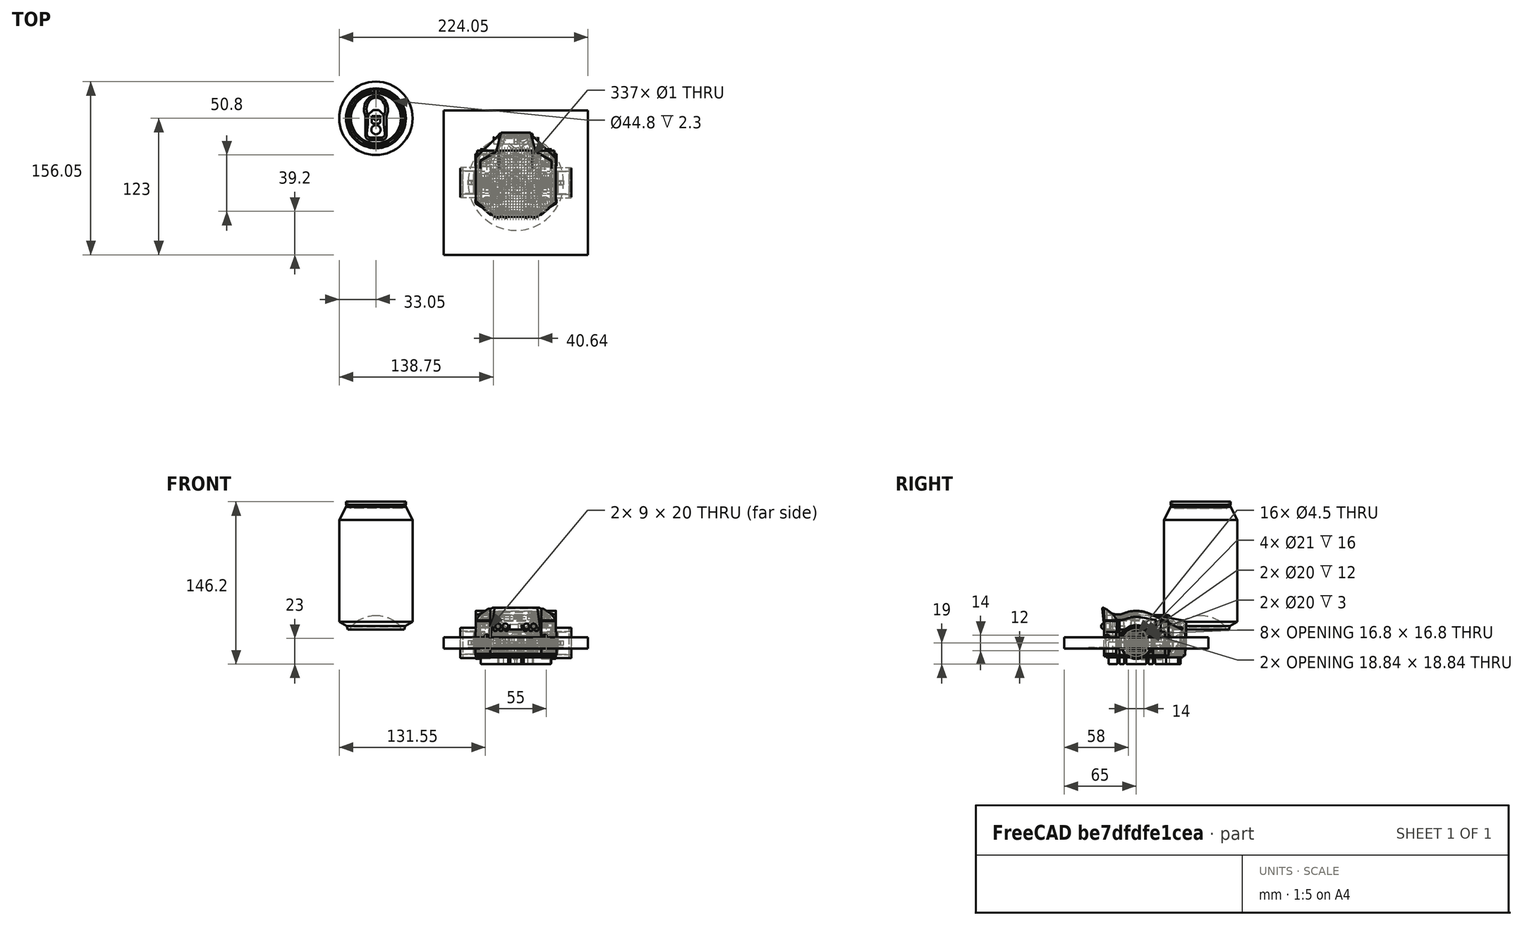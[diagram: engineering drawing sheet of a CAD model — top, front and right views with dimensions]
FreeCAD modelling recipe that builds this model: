
FCSTD DOCUMENT  (FreeCAD 0.16R)
Label: rat
License: All rights reserved
LicenseURL: http://en.wikipedia.org/wiki/All_rights_reserved
objects: Part::Cylinder×68, Part::MultiFuse×43, Part::Feature×36, Part::Cut×36, Sketcher::SketchObject×36, PartDesign::Pad×34, Part::FeaturePython×31, Part::Box×18, Part::Fillet×15, Part::Mirroring×12, Part::Chamfer×7, Part::MultiCommon×4, Image::ImagePlane×3, App::DocumentObjectGroup×3, Part::Sphere×1, Part::Compound×1
note: 376 computed .brp shape members not serialized (recipe doc carries the construction recipe); baked Part::Feature solids carry a one-line shape summary decoded from their .brp

FEATURE [Part::Feature] Part__Feature  label="Pololu - 1_250 Micro gear motor"
  shape: bbox 12 x 10 x 1 mm, 20 faces (baked)
FEATURE [Part::Feature] Part__Feature001  label="Pololu - 1_250 Micro gear motor001"
  shape: bbox 1 x 1 x 8 mm, 7 faces (baked)
FEATURE [Part::Feature] Part__Feature002  label="Pololu - 1_250 Micro gear motor002"
  shape: bbox 1 x 1 x 8 mm, 7 faces (baked)
FEATURE [Part::Feature] Part__Feature003  label="Pololu - 1_250 Micro gear motor003"
  shape: bbox 2 x 2 x 3 mm, 6 faces (baked)
FEATURE [Part::Feature] Part__Feature004  label="Pololu - 1_250 Micro gear motor004"
  shape: bbox 3 x 3 x 2 mm, 6 faces (baked)
FEATURE [Part::Feature] Part__Feature005  label="Pololu - 1_250 Micro gear motor005"
  shape: bbox 3 x 3 x 2 mm, 6 faces (baked)
FEATURE [Part::Feature] Part__Feature006  label="Pololu - 1_250 Micro gear motor006"
  shape: bbox 3 x 3 x 4 mm, 6 faces (baked)
FEATURE [Part::Feature] Part__Feature007  label="Pololu - 1_250 Micro gear motor007"
  shape: bbox 3 x 3 x 4 mm, 6 faces (baked)
FEATURE [Part::Feature] Part__Feature008  label="Pololu - 1_250 Micro gear motor008"
  shape: bbox 2 x 2 x 1.5 mm, 6 faces (baked)
FEATURE [Part::Feature] Part__Feature009  label="Pololu - 1_250 Micro gear motor009"
  shape: bbox 5.5 x 5.5 x 0.75 mm, 6 faces (baked)
FEATURE [Part::Feature] Part__Feature010  label="Pololu - 1_250 Micro gear motor010"
  shape: bbox 12 x 10 x 1 mm, 22 faces (baked)
FEATURE [Part::Feature] Part__Feature011  label="Pololu - 1_250 Micro gear motor011"
  shape: bbox 5.5 x 5.5 x 1 mm, 6 faces (baked)
FEATURE [Part::Feature] Part__Feature012  label="Pololu - 1_250 Micro gear motor012"
  shape: bbox 5.5 x 5.5 x 0.75 mm, 6 faces (baked)
FEATURE [Part::Feature] Part__Feature013  label="Pololu - 1_250 Micro gear motor013"
  shape: bbox 2 x 2 x 1.15 mm, 6 faces (baked)
FEATURE [Part::Feature] Part__Feature014  label="Pololu - 1_250 Micro gear motor014"
  shape: bbox 5.5 x 5.5 x 1 mm, 6 faces (baked)
FEATURE [Part::Feature] Part__Feature015  label="Pololu - 1_250 Micro gear motor015"
  shape: bbox 2 x 2 x 1.3 mm, 6 faces (baked)
FEATURE [Part::Feature] Part__Feature016  label="Pololu - 1_250 Micro gear motor016"
  shape: bbox 2.94 x 2.94 x 18.27 mm, 12 faces (baked)
FEATURE [Part::Feature] Part__Feature017  label="Pololu - 1_250 Micro gear motor017"
  shape: bbox 12 x 10 x 1.6 mm, 37 faces (baked)
FEATURE [Part::Feature] Part__Feature018  label="Pololu - 1_250 Micro gear motor018"
  shape: bbox 12 x 10 x 14 mm, 11 faces (baked)
FEATURE [Part::Feature] Part__Feature019  label="Pololu - 1_250 Micro gear motor019"
  shape: bbox 12 x 10 x 2.5 mm, 14 faces (baked)
FEATURE [Part::Feature] Part__Feature020  label="Pololu - 1_250 Micro gear motor020"
  shape: bbox 0.3 x 1.5 x 2 mm, 8 faces (baked)
FEATURE [Part::Feature] Part__Feature021  label="Pololu - 1_250 Micro gear motor021"
  shape: bbox 0.3 x 1.5 x 2 mm, 8 faces (baked)
FEATURE [Part::Feature] Part__Feature022  label="Pololu - 1_250 Micro gear motor022"
  shape: bbox 2.65 x 2.65 x 8.95 mm, 21 faces (baked)
FEATURE [Part::Feature] Part__Feature023  label="Pololu - 1_250 Micro gear motor023"
  shape: bbox 2.65 x 2.65 x 8.95 mm, 21 faces (baked)
FEATURE [Part::MultiFuse] Fusion  label="motor-src"
  Shapes = -> [Part__Feature,Part__Feature001,Part__Feature002,Part__Feature003,Part__Feature004,Part__Feature005,Part__Feature006,Part__Feature007,Part__Feature008,Part__Feature009,Part__Feature010,Part__Feature011,Part__Feature012,Part__Feature013,Part__Feature014,Part__Feature015,Part__Feature016,Part__Feature017,Part__Feature018,Part__Feature019,Part__Feature020,Part__Feature021,Part__Feature022,+1 more]
FEATURE [Part::FeaturePython] Clone  label="left-motor"  # Draft clone (typed FeaturePython)
  Objects = -> [Fusion]
  Placement = pos=(-14.5,0,5) rot=(0,-1,0;1.5708rad)
  Scale = (1,1,1)
FEATURE [Part::FeaturePython] Clone001  label="right-motor"  # Draft clone (typed FeaturePython)
  Objects = -> [Fusion]
  Placement = pos=(14.5,0,5) rot=(0,1,0;1.5708rad)
  Scale = (1,1,1)
FEATURE [Part::Cylinder] Cylinder
  Angle = 360
  Height = 16
  Radius = 13.75
FEATURE [Part::Cylinder] Cylinder001
  Angle = 360
  Height = 20
  Placement = pos=(0,0,-1) rot=(0,0,1;0rad)
  Radius = 10.5
FEATURE [Part::Cut] Cut
  Base = -> Cylinder
  Tool = -> Cylinder001
FEATURE [Part::Fillet] Fillet  label="tire-src"
  Base = -> Cut
  Edges = 2 edges r=1: [Edge1,Edge3]
FEATURE [Part::Cylinder] Cylinder002
  Angle = 360
  Height = 16
  Radius = 10.5
FEATURE [Part::Cylinder] Cylinder003
  Angle = 360
  Height = 16
  Placement = pos=(0,0,4) rot=(0,0,1;0rad)
  Radius = 9.8
FEATURE [Part::Cut] Cut001
  Base = -> Cylinder002
  Tool = -> Cylinder003
FEATURE [Part::FeaturePython] Clone002  label="Clone of tire-src"  # Draft clone (typed FeaturePython)
  Objects = -> [Fillet]
  Placement = pos=(-32,0,5) rot=(0,-1,0;1.5708rad)
  Scale = (1,1,1)
FEATURE [Part::FeaturePython] Clone004  label="Clone of tire-src001"  # Draft clone (typed FeaturePython)
  Objects = -> [Fillet]
  Placement = pos=(32,0,5) rot=(0,1,0;1.5708rad)
  Scale = (1,1,1)
FEATURE [Part::Box] Box  label="Cube"
  Height = 10
  Length = 130
  Placement = pos=(-65,-65,0) rot=(0,0,1;0rad)
  Width = 130
FEATURE [Part::Cylinder] Cylinder004
  Angle = 360
  Height = 1
  Radius = 43
FEATURE [Part::Feature] Part__Feature024  label="felga_solarbotics"
  shape: bbox 20.38 x 20.38 x 13.12 mm, 25 faces (baked)
FEATURE [Part::Feature] Part__Feature025  label="opona solarbotics"
  shape: bbox 28.6 x 28.6 x 12.96 mm, 18 faces (baked)
FEATURE [Part::FeaturePython] Clone006  label="left_wheel"  # Draft clone (typed FeaturePython)
  Objects = -> [Part__Feature024]
  Placement = pos=(-36,0,5) rot=(0,1,0;1.5708rad)
  Scale = (1,1,1)
FEATURE [Part::FeaturePython] Clone007  label="left_tire"  # Draft clone (typed FeaturePython)
  Objects = -> [Part__Feature025]
  Placement = pos=(-36,0,5) rot=(0,1,0;1.5708rad)
  Scale = (1,1,1)
FEATURE [Part::FeaturePython] Clone008  label="right_wheel"  # Draft clone (typed FeaturePython)
  Objects = -> [Part__Feature024]
  Placement = pos=(36,0,5) rot=(0,-1,0;1.5708rad)
  Scale = (1,1,1)
FEATURE [Part::FeaturePython] Clone009  label="right_tire"  # Draft clone (typed FeaturePython)
  Objects = -> [Part__Feature025]
  Placement = pos=(36,0,5) rot=(0,-1,0;1.5708rad)
  Scale = (1,1,1)
FEATURE [Part::Box] Box001  label="Cubo"
  Height = 17
  Length = 44
  Width = 12
FEATURE [Part::Box] Box002  label="Cube001"
  Height = 9
  Length = 22
  Placement = pos=(-11,-27.5,16) rot=(0,0,1;0rad)
  Width = 52
FEATURE [Sketcher::SketchObject] Sketch
  Placement = pos=(0,0,-6) rot=(0,0,1;0rad)
  sketch-geometry (23):
    g0: LineSegment StartX=-36.5 StartY=15 StartZ=0 EndX=-23 EndY=15 EndZ=0
    g1: LineSegment StartX=-23 StartY=15 StartZ=0 EndX=-23 EndY=-15 EndZ=0
    g2: LineSegment StartX=-23 StartY=-15 StartZ=0 EndX=-36.5 EndY=-15 EndZ=0
    g3: LineSegment StartX=36.5 StartY=-15 StartZ=0 EndX=23 EndY=-15 EndZ=0
    g4: LineSegment StartX=23 StartY=-15 StartZ=0 EndX=23 EndY=15 EndZ=0
    g5: LineSegment StartX=23 StartY=15 StartZ=0 EndX=36.5 EndY=15 EndZ=0
    g6: LineSegment [constr] StartX=-23 StartY=15 StartZ=0 EndX=23 EndY=15 EndZ=0
    g7: LineSegment [constr] StartX=-23 StartY=-15 StartZ=0 EndX=23 EndY=-15 EndZ=0
    g8: LineSegment StartX=-36.5 StartY=25.9507 StartZ=0 EndX=-24.3352 EndY=25.9507 EndZ=0
    g9: LineSegment StartX=-24.3352 StartY=25.9507 StartZ=0 EndX=-15 EndY=31.9395 EndZ=0
    g10: LineSegment StartX=15 StartY=31.9395 StartZ=0 EndX=24.3352 EndY=25.9507 EndZ=0
    g11: LineSegment StartX=24.3352 StartY=25.9507 StartZ=0 EndX=36.5 EndY=25.9507 EndZ=0
    g12: LineSegment [constr] StartX=-24.3352 StartY=25.9507 StartZ=0 EndX=24.3352 EndY=25.9507 EndZ=0
    g13: LineSegment StartX=-36.5 StartY=15 StartZ=0 EndX=-36.5 EndY=25.9507 EndZ=0
    g14: LineSegment StartX=-36.5 StartY=-15 StartZ=0 EndX=-36.5 EndY=-18.3134 EndZ=0
    g15: LineSegment StartX=36.5 StartY=25.9507 StartZ=0 EndX=36.5 EndY=15 EndZ=0
    g16: LineSegment StartX=-36.5 StartY=-18.3134 StartZ=0 EndX=-23 EndY=-26.9899 EndZ=0
    g17: LineSegment StartX=-23 StartY=-26.9899 StartZ=0 EndX=23 EndY=-26.9899 EndZ=0
    g18: LineSegment StartX=23 StartY=-26.9899 StartZ=0 EndX=36.5 EndY=-18.3134 EndZ=0
    g19: LineSegment StartX=36.5 StartY=-18.3134 StartZ=0 EndX=36.5 EndY=-15 EndZ=0
    g20: LineSegment StartX=-15 StartY=31.9395 StartZ=0 EndX=-15 EndY=44 EndZ=0
    g21: LineSegment StartX=-15 StartY=44 StartZ=0 EndX=15 EndY=44 EndZ=0
    g22: LineSegment StartX=15 StartY=44 StartZ=0 EndX=15 EndY=31.9395 EndZ=0
  constraints (61):
    c: Horizontal(g0)
    c: Coincident(g0,g1)
    c: Vertical(g1)
    c: Coincident(g1,g2)
    c: Horizontal(g2)
    c: Horizontal(g3)
    c: Coincident(g3,g4)
    c: Vertical(g4)
    c: Coincident(g4,g5)
    c: Horizontal(g5)
    c: Coincident(g6,g0)
    c: Coincident(g6,g4)
    c: Coincident(g7,g1)
    c: Horizontal(g7)
    c: Coincident(g7,g3)
    c: Equal(g1,g4)
    c: Distance(g4) = 30
    c: Symmetric(g4,g3,g-1)
    c: Distance(g0,g4) = 46
    c: Equal(g0,g5)
    c: Distance(g0) = 13.5
    c: Symmetric(g4,g0,g-2)
    c: Coincident(g8,g9)
    c: Coincident(g10,g11)
    c: Horizontal(g11)
    c: Horizontal(g8)
    c: Equal(g8,g11)
    c: Coincident(g12,g8)
    c: Coincident(g12,g10)
    c: Horizontal(g12)
    c: Symmetric(g8,g10,g-2)
    c: Symmetric(g9,g10,g-2)
    c: Equal(g3,g2)
    c: Equal(g2,g0)
    c: Coincident(g13,g0)
    c: Vertical(g13)
    c: Coincident(g2,g14)
    c: Vertical(g14)
    c: Coincident(g15,g5)
    c: Vertical(g15)
    c: Coincident(g11,g15)
    c: Coincident(g8,g13)
    c: Coincident(g14,g16)
    c: Coincident(g16,g17)
    c: Horizontal(g17)
    c: Coincident(g17,g18)
    c: Coincident(g18,g19)
    c: Vertical(g19)
    c: Coincident(g19,g3)
    c: Equal(g16,g18)
    c: Equal(g14,g19)
    c: Distance(g17) = 46
    c: Coincident(g9,g20)
    c: Vertical(g20)
    c: Coincident(g20,g21)
    c: Horizontal(g21)
    c: Coincident(g21,g22)
    c: Coincident(g22,g10)
    c: Vertical(g22)
    c: Distance(g21) = 30
    c: DistanceY(g-1,g20) = 44
FEATURE [PartDesign::Pad] Pad001
  Length = 21
  Length2 = 100
  Placement = pos=(0,0,-6) rot=(0,0,1;0rad)
  Sketch = -> Sketch
  Type = 0
FEATURE [Part::Cylinder] Cylinder005
  Angle = 360
  Height = 40
  Placement = pos=(-20,38,0) rot=(0,1,0;1.5708rad)
  Radius = 3
FEATURE [Part::Cylinder] Cylinder006
  Angle = 360
  Height = 40
  Placement = pos=(-20,38,9) rot=(0,1,0;1.5708rad)
  Radius = 3
FEATURE [Part::Cylinder] Cylinder007
  Angle = 360
  Height = 30
  Placement = pos=(-30,0,9) rot=(-1,0,0;1.5708rad)
  Radius = 3
FEATURE [Part::Cylinder] Cylinder008
  Angle = 360
  Height = 30
  Placement = pos=(-30,0,0) rot=(-1,0,0;1.5708rad)
  Radius = 3
FEATURE [Part::Cylinder] Cylinder009
  Angle = 360
  Height = 30
  Placement = pos=(30,0,9) rot=(-1,0,0;1.5708rad)
  Radius = 3
FEATURE [Part::Cylinder] Cylinder010
  Angle = 360
  Height = 30
  Placement = pos=(30,0,0) rot=(-1,0,0;1.5708rad)
  Radius = 3
FEATURE [Part::Cylinder] Cylinder011
  Angle = 360
  Height = 35
  Placement = pos=(7,16,9) rot=(-0.357407,0.862856,0.357407;1.71777rad)
  Radius = 3
FEATURE [Part::Cylinder] Cylinder012
  Angle = 360
  Height = 35
  Placement = pos=(7,16,0) rot=(-0.357407,0.862856,0.357407;1.71777rad)
  Radius = 3
FEATURE [Part::Cylinder] Cylinder013
  Angle = 360
  Height = 35
  Placement = pos=(-7,16,9) rot=(0.678599,-0.281084,-0.678598;3.68963rad)
  Radius = 3
FEATURE [Part::Cylinder] Cylinder014
  Angle = 360
  Height = 35
  Placement = pos=(-7,16,0) rot=(-0.678598,0.281085,0.678598;2.59356rad)
  Radius = 3
FEATURE [Part::MultiFuse] Fusion001
  Shapes = -> [Cylinder009,Cylinder013,Cylinder010,Cylinder012,Cylinder006,Cylinder008,Cylinder011,Cylinder005,Cylinder014,Cylinder007]
FEATURE [Part::Cut] Cut003
  Base = -> Pad001
  Tool = -> Fusion001
FEATURE [Part::Cylinder] Cylinder015  label="Cilindro"
  Angle = 360
  Height = 6.2
  Radius = 2.5
FEATURE [Part::Sphere] Sphere  label="Esféra"
  Angle1 = -90
  Angle2 = 90
  Angle3 = 180
  Placement = pos=(0,0,6.2) rot=(1,0,0;1.5708rad)
  Radius = 2.5
FEATURE [Part::Cylinder] Cylinder016  label="Cilindro001"
  Angle = 360
  Height = 1
  Radius = 2.9
FEATURE [Part::MultiFuse] Fusion002  label="Funda"
  Shapes = -> [Cylinder015,Cylinder016,Sphere]
FEATURE [Sketcher::SketchObject] Sketch002
  Placement = pos=(0,0,0) rot=(1,0,0;1.5708rad)
  sketch-geometry (9):
    g0: LineSegment StartX=-2.06901 StartY=-1.50757 StartZ=0 EndX=-2.06901 EndY=2.25482 EndZ=0
    g1: LineSegment StartX=-2.06901 StartY=2.25482 StartZ=0 EndX=-1.71216 EndY=2.25482 EndZ=0
    g2: LineSegment StartX=-1.71216 StartY=2.25482 StartZ=0 EndX=-1.71216 EndY=3.41819 EndZ=0
    g3: LineSegment StartX=-1.71216 StartY=3.41819 StartZ=0 EndX=1.35716 EndY=3.41819 EndZ=0
    g4: LineSegment StartX=1.35716 StartY=3.41819 StartZ=0 EndX=1.35716 EndY=3.07166 EndZ=0
    g5: LineSegment StartX=1.35716 StartY=3.07166 StartZ=0 EndX=-0.05374 EndY=1.66076 EndZ=0
    g6: LineSegment StartX=-0.05374 StartY=1.66076 StartZ=0 EndX=-1.56901 EndY=1.66076 EndZ=0
    g7: LineSegment StartX=-1.56901 StartY=1.66076 StartZ=0 EndX=-1.56901 EndY=-1.5 EndZ=0
    g8: LineSegment StartX=-1.56901 StartY=-1.5 StartZ=0 EndX=-2.06901 EndY=-1.50757 EndZ=0
  constraints (18):
    c: Vertical(g0)
    c: Coincident(g0,g1)
    c: Horizontal(g1)
    c: Coincident(g1,g2)
    c: Vertical(g2)
    c: Coincident(g2,g3)
    c: Horizontal(g3)
    c: Coincident(g3,g4)
    c: Vertical(g4)
    c: Coincident(g4,g5)
    c: Coincident(g5,g6)
    c: Horizontal(g6)
    c: Coincident(g6,g7)
    c: Vertical(g7)
    c: Coincident(g7,g8)
    c: Coincident(g8,g0)
    c: DistanceY(g-1,g7) = -1.5
    c: DistanceX(g0,g7) = 0.5
FEATURE [PartDesign::Pad] Pad002  label="Catodo"
  Length = 0.3
  Length2 = 100
  Placement = pos=(0,0,0) rot=(1,0,0;1.5708rad)
  Sketch = -> Sketch002
  Type = 0
FEATURE [Sketcher::SketchObject] Sketch003
  Placement = pos=(0,0,0) rot=(1,0,0;1.5708rad)
  sketch-geometry (7):
    g0: LineSegment StartX=2.0234 StartY=-1.57582 StartZ=0 EndX=2.0234 EndY=3.38927 EndZ=0
    g1: LineSegment StartX=2.0234 StartY=3.38927 StartZ=0 EndX=1.5234 EndY=3.36901 EndZ=0
    g2: LineSegment StartX=1.5234 StartY=3.36901 StartZ=0 EndX=1.5234 EndY=3.02449 EndZ=0
    g3: LineSegment StartX=1.5234 StartY=3.02449 StartZ=0 EndX=0.294592 EndY=1.68695 EndZ=0
    g4: LineSegment StartX=0.294592 StartY=1.68695 StartZ=0 EndX=1.51053 EndY=1.68695 EndZ=0
    g5: LineSegment StartX=1.51053 StartY=1.68695 StartZ=0 EndX=1.51053 EndY=-1.57582 EndZ=0
    g6: LineSegment StartX=1.51053 StartY=-1.57582 StartZ=0 EndX=2.0234 EndY=-1.57582 EndZ=0
  constraints (13):
    c: Vertical(g0)
    c: Coincident(g1,g0)
    c: DistanceX(g1,g0) = 0.5
    c: Coincident(g1,g2)
    c: Vertical(g2)
    c: Coincident(g2,g3)
    c: Coincident(g3,g4)
    c: Horizontal(g4)
    c: Coincident(g4,g5)
    c: Vertical(g5)
    c: Coincident(g5,g6)
    c: Coincident(g6,g0)
    c: Horizontal(g6)
FEATURE [PartDesign::Pad] Pad003  label="Anodo"
  Length = 0.3
  Length2 = 100
  Placement = pos=(0,0,0) rot=(1,0,0;1.5708rad)
  Sketch = -> Sketch003
  Type = 0
FEATURE [Part::MultiFuse] Fusion003  label="led-src"
  Shapes = -> [Fusion002,Pad003,Pad002]
FEATURE [Part::Box] Box003  label="Cube002"
  Height = 16
  Length = 30
  Placement = pos=(-15,-27,14) rot=(0,0,1;0rad)
  Width = 71
FEATURE [Part::Chamfer] Chamfer
  Base = -> Box003
  Edges = 1 edges r=15: [Edge12]
FEATURE [Part::MultiFuse] Fusion004
  Shapes = -> [Chamfer,Cut003]
FEATURE [Part::FeaturePython] Clone019  label="clone-lid"  # WARN: FeaturePython — macro-defined, semantics opaque (R4)
  Placement = pos=(0,0,110.4) rot=(0,0,1;3.14159rad)
  Scale = (1,1,1)
FEATURE [Part::FeaturePython] Clone020  label="clone-can"  # WARN: FeaturePython — macro-defined, semantics opaque (R4)
  Placement = pos=(0,0,0) rot=(1,0,0;1.5708rad)
  Scale = (1,1,1)
FEATURE [Sketcher::SketchObject] Sketch006
  Placement = pos=(36,0,1) rot=(0.57735,0.57735,0.57735;2.0944rad)
  sketch-geometry (9):
    g0: LineSegment StartX=-29 StartY=36 StartZ=0 EndX=-29 EndY=-8 EndZ=0
    g1: LineSegment StartX=-29 StartY=-8 StartZ=0 EndX=43 EndY=-8 EndZ=0
    g2: LineSegment StartX=43 StartY=-8 StartZ=0 EndX=45 EndY=0 EndZ=0
    g3: LineSegment StartX=45 StartY=0 StartZ=0 EndX=45 EndY=20.5618 EndZ=0
    g4: LineSegment StartX=41.7004 StartY=24.5 StartZ=0 EndX=4.63982 EndY=31.0907 EndZ=0
    g5: LineSegment StartX=-23.2217 StartY=31.5389 StartZ=0 EndX=-29 EndY=36 EndZ=0
    g6: ArcOfCircle CenterX=-14.819 CenterY=42.4227 CenterZ=0 NormalX=0 NormalY=0 NormalZ=1 Radius=13.75 StartAngle=4.05493 EndAngle=5.08943
    g7: ArcOfCircle CenterX=0 CenterY=5 CenterZ=0 NormalX=0 NormalY=0 NormalZ=1 Radius=26.5 StartAngle=1.3948 EndAngle=1.94784
    g8: ArcOfCircle CenterX=41 CenterY=20.5618 CenterZ=0 NormalX=0 NormalY=0 NormalZ=1 Radius=4 StartAngle=0 EndAngle=1.3948
  constraints (28):
    c: Vertical(g0)
    c: Coincident(g0,g1)
    c: Horizontal(g1)
    c: Coincident(g1,g2)
    c: Tangent(g5,g6)
    c: Coincident(g6,g7)
    c: Tangent(g6,g7)
    c: DistanceY(g0,g5) = 44
    c: DistanceY(g0,g-1) = 8
    c: Coincident(g7,g4)
    c: Tangent(g7,g4)
    c: PointOnObject(g7,g-2)
    c: Distance(g-1,g7) = 5
    c: Coincident(g5,g6)
    c: Tangent(g4,g8) = -1.5708
    c: Tangent(g3,g8) = -1.5708
    c: Vertical(g3)
    c: Coincident(g0,g5)
    c: DistanceX(g0,g-1) = 29
    c: DistanceX(g-1,g3) = 45
    c: Distance(g1) = 72
    c: Coincident(g2,g3)
    c: DistanceY(g2,g-1) = 0
    c: Radius(g8) = 4
    c: Radius(g7) = 26.5
    c: Radius(g6) = 13.75
    c: Distance(g5) = 7.3
    c: DistanceY(g-1,g4) = 24.5
FEATURE [PartDesign::Pad] Pad004
  Length = 72
  Length2 = 100
  Placement = pos=(36,0,1) rot=(0.57735,0.57735,0.57735;2.0944rad)
  Reversed = true
  Sketch = -> Sketch006
  Type = 0
FEATURE [Sketcher::SketchObject] Sketch007
  Placement = pos=(0,0,60) rot=(0,0,1;0rad)
  sketch-geometry (14):
    g0: LineSegment StartX=37 StartY=17 StartZ=0 EndX=37 EndY=-17 EndZ=0
    g1: LineSegment StartX=-37 StartY=-17 StartZ=0 EndX=-37 EndY=17 EndZ=0
    g2: LineSegment StartX=-37 StartY=-17 StartZ=0 EndX=-18.8423 EndY=-28.6318 EndZ=0
    g3: LineSegment StartX=18.8423 StartY=-28.6319 StartZ=0 EndX=37 EndY=-17 EndZ=0
    g4: LineSegment StartX=-37 StartY=17 StartZ=0 EndX=-17.5551 EndY=28 EndZ=0
    g5: LineSegment StartX=-17.5551 StartY=28 StartZ=0 EndX=-13 EndY=45 EndZ=0
    g6: LineSegment StartX=-13 StartY=45 StartZ=0 EndX=13 EndY=45 EndZ=0
    g7: LineSegment StartX=13 StartY=45 StartZ=0 EndX=17.5551 EndY=28 EndZ=0
    g8: LineSegment StartX=17.5551 StartY=28 StartZ=0 EndX=37 EndY=17 EndZ=0
    g9: ArcOfCircle CenterX=-21 CenterY=-32 CenterZ=0 NormalX=0 NormalY=0 NormalZ=1 Radius=4 StartAngle=0 EndAngle=1.00105
    g10: ArcOfCircle CenterX=21 CenterY=-32 CenterZ=0 NormalX=0 NormalY=0 NormalZ=1 Radius=4 StartAngle=2.14054 EndAngle=3.14159
    g11: LineSegment StartX=-17 StartY=-32 StartZ=0 EndX=17 EndY=-32 EndZ=0
    g12: LineSegment [constr] StartX=-37 StartY=17 StartZ=0 EndX=37 EndY=17 EndZ=0
    g13: LineSegment [constr] StartX=-17.5551 StartY=28 StartZ=0 EndX=17.5551 EndY=28 EndZ=0
  constraints (42):
    c: Coincident(g4,g5)
    c: Coincident(g5,g6)
    c: Horizontal(g6)
    c: Coincident(g6,g7)
    c: Coincident(g7,g8)
    c: Coincident(g0,g8)
    c: Coincident(g1,g4)
    c: Coincident(g9,g2)
    c: Coincident(g10,g3)
    c: Coincident(g11,g9)
    c: Coincident(g11,g10)
    c: Horizontal(g11)
    c: Tangent(g2,g9)
    c: Tangent(g3,g10)
    c: Symmetric(g9,g10,g-2)
    c: Radius(g9) = 4
    c: Equal(g9,g10)
    c: Equal(g3,g2)
    c: DistanceY(g10,g-1) = 32
    c: Vertical(g1)
    c: Vertical(g0)
    c: DistanceY(g9,g5) = 77
    c: DistanceX(g1,g0) = 74
    c: Equal(g1,g0)
    c: Equal(g4,g8)
    c: Coincident(g12,g1)
    c: Coincident(g12,g0)
    c: Horizontal(g12)
    c: Equal(g5,g7)
    c: DistanceX(g1,g-1) = 37
    c: Distance(g6) = 26
    c: DistanceY(g-1,g1) = 17
    c: DistanceY(g-1,g7) = 28
    c: Coincident(g0,g3)
    c: Coincident(g1,g2)
    c: Distance(g1) = 34
    c: Perpendicular(g9,g11)
    c: Distance(g11) = 34
    c: Angle(g5,g6) = 1.8326
    c: Coincident(g13,g4)
    c: Coincident(g13,g7)
    c: Horizontal(g13)
FEATURE [Sketcher::SketchObject] Sketch008
  Placement = pos=(40,0,0) rot=(0.57735,0.57735,0.57735;2.0944rad)
  sketch-geometry (5):
    g0: LineSegment StartX=-15.5 StartY=17 StartZ=0 EndX=-15.5 EndY=-15 EndZ=0
    g1: LineSegment StartX=-15.5 StartY=-15 StartZ=0 EndX=15.5 EndY=-15 EndZ=0
    g2: LineSegment StartX=15.5 StartY=-15 StartZ=0 EndX=15.5 EndY=4.99997 EndZ=0
    g3: ArcOfCircle CenterX=0 CenterY=5 CenterZ=0 NormalX=0 NormalY=0 NormalZ=1 Radius=15.5 StartAngle=6.28318 EndAngle=8.53934
    g4: LineSegment StartX=-9.81075 StartY=17 StartZ=0 EndX=-15.5 EndY=17 EndZ=0
  constraints (16):
    c: Vertical(g0)
    c: Coincident(g0,g1)
    c: Horizontal(g1)
    c: Coincident(g1,g2)
    c: PointOnObject(g3,g-2)
    c: Coincident(g3,g2)
    c: Tangent(g2,g3)
    c: Vertical(g2)
    c: Distance(g-1,g3) = 5
    c: Radius(g3) = 15.5
    c: Distance(g2) = 20
    c: Coincident(g4,g3)
    c: Coincident(g4,g0)
    c: Horizontal(g4)
    c: Distance(g1) = 31
    c: Distance(g0) = 32
FEATURE [PartDesign::Pad] Pad006
  Length = 18
  Length2 = 100
  Placement = pos=(40,0,0) rot=(0.57735,0.57735,0.57735;2.0944rad)
  Reversed = true
  Sketch = -> Sketch008
  Type = 0
FEATURE [Part::FeaturePython] Clone027  label="Clone of Fillet005"  # WARN: FeaturePython — macro-defined, semantics opaque (R4)
  Scale = (1,1,1)
FEATURE [Part::Cylinder] Cylinder017
  Angle = 360
  Height = 40
  Placement = pos=(-20,38,0) rot=(0,1,0;1.5708rad)
  Radius = 3
FEATURE [Part::Cylinder] Cylinder018
  Angle = 360
  Height = 40
  Placement = pos=(-20,38,9) rot=(0,1,0;1.5708rad)
  Radius = 3
FEATURE [Part::Cylinder] Cylinder019
  Angle = 360
  Height = 30
  Placement = pos=(-29,0,9) rot=(-1,0,0;1.5708rad)
  Radius = 3
FEATURE [Part::Cylinder] Cylinder020
  Angle = 360
  Height = 30
  Placement = pos=(-29,0,0) rot=(-1,0,0;1.5708rad)
  Radius = 3
FEATURE [Part::Cylinder] Cylinder021
  Angle = 360
  Height = 30
  Placement = pos=(29,0,9) rot=(-1,0,0;1.5708rad)
  Radius = 3
FEATURE [Part::Cylinder] Cylinder022
  Angle = 360
  Height = 30
  Placement = pos=(29,0,0) rot=(-1,0,0;1.5708rad)
  Radius = 3
FEATURE [Part::Box] Box004  label="Cube003"
  Height = 27
  Length = 10.8
  Width = 8
FEATURE [Part::MultiFuse] Fusion006
  Shapes = -> [Cylinder019,Cylinder021,Cylinder022,Cylinder018,Cylinder020,Cylinder017]
FEATURE [Sketcher::SketchObject] Sketch011
  Placement = pos=(0,-20,0) rot=(1,0,0;1.5708rad)
  sketch-geometry (2):
    g0: Circle CenterX=2.1 CenterY=24.9 CenterZ=0 NormalX=0 NormalY=0 NormalZ=1 Radius=1.1
    g1: Circle CenterX=8.7 CenterY=2.1 CenterZ=0 NormalX=0 NormalY=0 NormalZ=1 Radius=1.1
  constraints (6):
    c: Radius(g1) = 1.1
    c: Equal(g1,g0)
    c: DistanceX(g-1,g0) = 2.1
    c: DistanceY(g-1,g0) = 24.9
    c: DistanceY(g-1,g1) = 2.1
    c: DistanceX(g-1,g1) = 8.7
FEATURE [PartDesign::Pad] Pad007
  Length = 45
  Length2 = 100
  Placement = pos=(0,-20,0) rot=(1,0,0;1.5708rad)
  Reversed = true
  Sketch = -> Sketch011
  Type = 0
FEATURE [Sketcher::SketchObject] Sketch012
  Placement = pos=(0,20,0) rot=(0,0.707107,0.707107;3.14159rad)
  sketch-geometry (10):
    g0: ArcOfCircle CenterX=-2.1 CenterY=24.9 CenterZ=0 NormalX=0 NormalY=0 NormalZ=1 Radius=1.8 StartAngle=3.14159 EndAngle=4.71239
    g1: ArcOfCircle CenterX=-8.7 CenterY=2.1 CenterZ=0 NormalX=0 NormalY=0 NormalZ=1 Radius=1.8 StartAngle=9.53061e-06 EndAngle=1.57079
    g2: LineSegment StartX=-8.7 StartY=3.9 StartZ=0 EndX=-14.9 EndY=3.90001 EndZ=0
    g3: LineSegment StartX=-14.9 StartY=3.90001 StartZ=0 EndX=-14.9 EndY=-4.09998 EndZ=0
    g4: LineSegment StartX=-14.9 StartY=-4.09998 StartZ=0 EndX=-6.9 EndY=-4.09998 EndZ=0
    g5: LineSegment StartX=-6.9 StartY=-4.09998 StartZ=0 EndX=-6.9 EndY=2.10002 EndZ=0
    g6: LineSegment StartX=-3.9 StartY=24.9 StartZ=0 EndX=-3.9 EndY=31.1 EndZ=0
    g7: LineSegment StartX=-3.9 StartY=31.1 StartZ=0 EndX=4.1 EndY=31.1 EndZ=0
    g8: LineSegment StartX=4.1 StartY=31.1 StartZ=0 EndX=4.1 EndY=23.1 EndZ=0
    g9: LineSegment StartX=4.1 StartY=23.1 StartZ=0 EndX=-2.1 EndY=23.1 EndZ=0
  constraints (30):
    c: Tangent(g1,g2) = -1.5708
    c: Coincident(g2,g3)
    c: Vertical(g3)
    c: Coincident(g3,g4)
    c: Horizontal(g4)
    c: Coincident(g4,g5)
    c: Coincident(g5,g1)
    c: Vertical(g5)
    c: Tangent(g0,g6) = 1.5708
    c: Coincident(g6,g7)
    c: Horizontal(g7)
    c: Coincident(g7,g8)
    c: Vertical(g8)
    c: Coincident(g8,g9)
    c: Coincident(g9,g0)
    c: Horizontal(g9)
    c: Tangent(g1,g5)
    c: Vertical(g6)
    c: Equal(g2,g5)
    c: Equal(g5,g6)
    c: Equal(g6,g9)
    c: Equal(g3,g4)
    c: Equal(g1,g0)
    c: Tangent(g0,g9)
    c: DistanceX(g0,g-1) = 2.1
    c: DistanceY(g-1,g0) = 24.9
    c: DistanceX(g1,g-1) = 8.7
    c: DistanceY(g-1,g1) = 2.1
    c: Distance(g8) = 8
    c: DistanceY(g-1,g1) = 3.9
FEATURE [PartDesign::Pad] Pad008
  Length = 18.5
  Length2 = 100
  Placement = pos=(0,20,0) rot=(0,0.707107,0.707107;3.14159rad)
  Reversed = true
  Sketch = -> Sketch012
  Type = 0
FEATURE [Part::MultiFuse] Fusion007
  Shapes = -> [Pad007,Pad008]
FEATURE [Part::Box] Box005  label="Cube004"
  Height = 19.2
  Length = 8
  Placement = pos=(1.4,0,3.9) rot=(0,0,1;0rad)
  Width = 12
FEATURE [Part::Cut] Cut005
  Base = -> Box004
  Tool = -> Fusion007
FEATURE [Part::MultiFuse] Fusion008
  Shapes = -> [Cut005,Box005]
FEATURE [Part::FeaturePython] Clone030  label="Clone of Fusion008"  # Draft clone (typed FeaturePython)
  Objects = -> [Fusion008]
  Placement = pos=(22,17.1,-4.5) rot=(0,0,1;0rad)
  Scale = (1,1,1)
FEATURE [Part::FeaturePython] Clone031  label="Clone of Fusion009"  # Draft clone (typed FeaturePython)
  Objects = -> [Fusion008]
  Placement = pos=(-33,17.1,-4.5) rot=(0,0,1;0rad)
  Scale = (1,1,1)
FEATURE [Part::FeaturePython] Clone032  label="Clone of Fusion010"  # Draft clone (typed FeaturePython)
  Objects = -> [Fusion008]
  Placement = pos=(-5,29,-4.5) rot=(0,0,1;1.309rad)
  Scale = (1,1,1)
FEATURE [Part::Mirroring] Part__Mirroring  label="Clone of Fusion010 (Mirror #1)"
  Base = (0,0,0)
  Normal = (1,0,0)
  Source = -> Clone032
FEATURE [Part::MultiFuse] Fusion005  label="final-can"
  Placement = pos=(-126,58,17) rot=(0,0,1;0rad)
  Shapes = -> [Clone019,Clone020]
FEATURE [Part::Box] Box009  label="Cube008"
  Height = 31
  Length = 14.8
  Placement = pos=(-35,16,-8) rot=(0,0,1;0rad)
  Width = 13
FEATURE [Part::Box] Box010  label="Cube009"
  Height = 27
  Length = 10.8
  Placement = pos=(-33,28,-6) rot=(0,0,1;0rad)
  Width = 13
FEATURE [Part::Cut] Cut007
  Base = -> Box009
  Tool = -> Box010
FEATURE [Part::Fillet] Fillet006
  Base = -> Cut007
  Edges = 4 edges r=2: [Edge2,Edge4,Edge9,Edge16]
FEATURE [Part::Fillet] Fillet007
  Base = -> Fillet006
  Edges = 4 edges r=1: [Edge29,Edge30,Edge32,Edge34]
  Placement = pos=(55,0,1.5) rot=(0,0,1;0rad)
FEATURE [Sketcher::SketchObject] Sketch013
  Placement = pos=(0,0,-7) rot=(0,0,1;0rad)
  sketch-geometry (20):
    g0: LineSegment StartX=-36 StartY=-17.5 StartZ=0 EndX=-23 EndY=-29 EndZ=0
    g1: LineSegment StartX=23 StartY=-29 StartZ=0 EndX=36 EndY=-17.5 EndZ=0
    g2: LineSegment StartX=-36 StartY=17.5 StartZ=0 EndX=-17.75 EndY=28 EndZ=0
    g3: LineSegment StartX=-17.75 StartY=28 StartZ=0 EndX=-14.1997 EndY=41.25 EndZ=0
    g4: LineSegment StartX=-14.1997 StartY=41.25 StartZ=0 EndX=14.1997 EndY=41.25 EndZ=0
    g5: LineSegment StartX=14.1997 StartY=41.25 StartZ=0 EndX=17.75 EndY=28 EndZ=0
    g6: LineSegment StartX=17.75 StartY=28 StartZ=0 EndX=36 EndY=17.5 EndZ=0
    g7: LineSegment StartX=-23 StartY=-29 StartZ=0 EndX=23 EndY=-29 EndZ=0
    g8: LineSegment [constr] StartX=-36 StartY=17.5 StartZ=0 EndX=36 EndY=17.5 EndZ=0
    g9: LineSegment [constr] StartX=-17.75 StartY=28 StartZ=0 EndX=17.75 EndY=28 EndZ=0
    g10: LineSegment StartX=-36 StartY=17.5 StartZ=0 EndX=-36 EndY=15.5 EndZ=0
    g11: LineSegment StartX=-36 StartY=15.5 StartZ=0 EndX=-22 EndY=15.5 EndZ=0
    g12: LineSegment StartX=-22 StartY=15.5 StartZ=0 EndX=-22 EndY=-15.5 EndZ=0
    g13: LineSegment StartX=-22 StartY=-15.5 StartZ=0 EndX=-36 EndY=-15.5 EndZ=0
    g14: LineSegment StartX=-36 StartY=-15.5 StartZ=0 EndX=-36 EndY=-17.5 EndZ=0
    g15: LineSegment StartX=36 StartY=17.5 StartZ=0 EndX=36 EndY=15.5 EndZ=0
    g16: LineSegment StartX=36 StartY=15.5 StartZ=0 EndX=22 EndY=15.5 EndZ=0
    g17: LineSegment StartX=22 StartY=15.5 StartZ=0 EndX=22 EndY=-15.5 EndZ=0
    g18: LineSegment StartX=22 StartY=-15.5 StartZ=0 EndX=36 EndY=-15.5 EndZ=0
    g19: LineSegment StartX=36 StartY=-15.5 StartZ=0 EndX=36 EndY=-17.5 EndZ=0
  constraints (58):
    c: Coincident(g2,g3)
    c: Coincident(g3,g4)
    c: Horizontal(g4)
    c: Coincident(g4,g5)
    c: Coincident(g5,g6)
    c: Equal(g1,g0)
    c: DistanceX(g0,g1) = 72
    c: Equal(g2,g6)
    c: Horizontal(g8)
    c: Equal(g3,g5)
    c: DistanceX(g2,g-1) = 36
    c: DistanceY(g-1,g2) = 17.5
    c: DistanceY(g-1,g5) = 28
    c: Coincident(g9,g2)
    c: Coincident(g9,g5)
    c: Horizontal(g9)
    c: Coincident(g1,g7)
    c: Coincident(g0,g7)
    c: Horizontal(g7)
    c: Distance(g7) = 46
    c: DistanceY(g1,g4) = 70.25
    c: DistanceY(g0,g2) = 35
    c: Coincident(g2,g10)
    c: Vertical(g10)
    c: Coincident(g10,g11)
    c: Horizontal(g11)
    c: Coincident(g11,g12)
    c: Vertical(g12)
    c: Coincident(g12,g13)
    c: Horizontal(g13)
    c: Coincident(g13,g14)
    c: Coincident(g14,g0)
    c: Vertical(g14)
    c: Equal(g10,g14)
    c: Distance(g12) = 31
    c: Distance(g11) = 14
    c: Coincident(g6,g15)
    c: Vertical(g15)
    c: Coincident(g15,g16)
    c: Horizontal(g16)
    c: Coincident(g16,g17)
    c: Vertical(g17)
    c: Coincident(g17,g18)
    c: Coincident(g18,g19)
    c: Vertical(g19)
    c: Coincident(g1,g19)
    c: Horizontal(g18)
    c: Equal(g14,g15)
    c: Equal(g15,g19)
    c: Equal(g17,g12)
    c: Equal(g13,g18)
    c: Equal(g16,g11)
    c: Equal(g16,g18)
    c: Coincident(g8,g6)
    c: Coincident(g8,g2)
    c: Angle(g9,g3) = 1.309
    c: Distance(g9) = 35.5
    c: DistanceY(g0,g-1) = 29
FEATURE [PartDesign::Pad] Pad009
  Length = 2
  Length2 = 100
  Placement = pos=(0,0,-7) rot=(0,0,1;0rad)
  Sketch = -> Sketch013
  Type = 0
FEATURE [Sketcher::SketchObject] Sketch015
  Placement = pos=(-23,0,0) rot=(0.57735,0.57735,0.57735;2.0944rad)
  sketch-geometry (6):
    g0: ArcOfCircle CenterX=0 CenterY=6 CenterZ=0 NormalX=0 NormalY=0 NormalZ=1 Radius=7.2 StartAngle=3.90538 EndAngle=5.5194
    g1: LineSegment StartX=-5.2 StartY=1.02004 StartZ=0 EndX=-5.2 EndY=13.02 EndZ=0
    g2: LineSegment StartX=-5.2 StartY=13.02 StartZ=0 EndX=5.2 EndY=13.02 EndZ=0
    g3: LineSegment StartX=5.2 StartY=13.02 StartZ=0 EndX=5.2 EndY=1.02004 EndZ=0
    g4: LineSegment [constr] StartX=-5.2 StartY=1.02004 StartZ=0 EndX=5.2 EndY=1.02004 EndZ=0
    g5: GeomPoint [constr] X=0 Y=-1.2 Z=0
  constraints (17):
    c: Coincident(g1,g2)
    c: Horizontal(g2)
    c: Coincident(g2,g3)
    c: Vertical(g3)
    c: Vertical(g1)
    c: PointOnObject(g0,g-2)
    c: Distance(g1) = 12
    c: Coincident(g4,g0)
    c: Horizontal(g4)
    c: Coincident(g0,g1)
    c: Coincident(g0,g3)
    c: Coincident(g0,g4)
    c: Distance(g2) = 10.4
    c: PointOnObject(g5,g-2)
    c: PointOnObject(g5,g0)
    c: Distance(g-1,g5) = 1.2
    c: Distance(g-1,g0) = 6
FEATURE [PartDesign::Pad] Pad010
  Length = 46
  Length2 = 100
  Placement = pos=(-23,0,0) rot=(0.57735,0.57735,0.57735;2.0944rad)
  Sketch = -> Sketch015
  Type = 0
FEATURE [Sketcher::SketchObject] Sketch016
  Placement = pos=(0,0,11.2) rot=(0,0,1;0rad)
  sketch-geometry (18):
    g0: LineSegment [constr] StartX=-25 StartY=2 StartZ=0 EndX=-22 EndY=2 EndZ=0
    g1: LineSegment StartX=-22 StartY=2 StartZ=0 EndX=-22 EndY=11 EndZ=0
    g2: LineSegment StartX=-22 StartY=-11 StartZ=0 EndX=-22 EndY=-2 EndZ=0
    g3: LineSegment [constr] StartX=-22 StartY=-2 StartZ=0 EndX=-25 EndY=-2 EndZ=0
    g4: LineSegment [constr] StartX=-25 StartY=-2 StartZ=0 EndX=-25 EndY=2 EndZ=0
    g5: Circle CenterX=-19 CenterY=8 CenterZ=0 NormalX=0 NormalY=0 NormalZ=1 Radius=1.6
    g6: Circle CenterX=-19 CenterY=-8 CenterZ=0 NormalX=0 NormalY=0 NormalZ=1 Radius=1.6
    g7: LineSegment [constr] StartX=-19 StartY=-8 StartZ=0 EndX=-19 EndY=8 EndZ=0
    g8: LineSegment StartX=-22 StartY=11 StartZ=0 EndX=-18 EndY=11 EndZ=0
    g9: LineSegment StartX=-18 StartY=11 StartZ=0 EndX=-14 EndY=7 EndZ=0
    g10: LineSegment [constr] StartX=-14 StartY=7 StartZ=0 EndX=-14 EndY=-7 EndZ=0
    g11: LineSegment StartX=-14 StartY=-7 StartZ=0 EndX=-18 EndY=-11 EndZ=0
    g12: LineSegment StartX=-18 StartY=-11 StartZ=0 EndX=-22 EndY=-11 EndZ=0
    g13: LineSegment [constr] StartX=-18 StartY=11 StartZ=0 EndX=-18 EndY=-11 EndZ=0
    g14: LineSegment StartX=-14 StartY=7 StartZ=0 EndX=-7 EndY=7 EndZ=0
    g15: LineSegment StartX=-7 StartY=7 StartZ=0 EndX=-7 EndY=-7 EndZ=0
    g16: LineSegment StartX=-7 StartY=-7 StartZ=0 EndX=-14 EndY=-7 EndZ=0
    g17: LineSegment StartX=-22 StartY=2 StartZ=0 EndX=-22 EndY=-2 EndZ=0
  constraints (50):
    c: Horizontal(g0)
    c: Coincident(g0,g1)
    c: Vertical(g1)
    c: Vertical(g2)
    c: Coincident(g2,g3)
    c: Horizontal(g3)
    c: Coincident(g3,g4)
    c: Coincident(g4,g0)
    c: Vertical(g4)
    c: Equal(g0,g3)
    c: DistanceX(g3,g2) = 3
    c: Distance(g4) = 4
    c: Equal(g1,g2)
    c: DistanceX(g1,g-1) = 22
    c: Vertical(g7)
    c: Radius(g5) = 1.6
    c: Equal(g5,g6)
    c: Horizontal(g8)
    c: Coincident(g8,g9)
    c: Coincident(g9,g10)
    c: Vertical(g10)
    c: Coincident(g10,g11)
    c: Coincident(g11,g12)
    c: Horizontal(g12)
    c: Coincident(g2,g12)
    c: Angle(g10,g11) = 2.35619
    c: Coincident(g1,g8)
    c: Equal(g9,g11)
    c: DistanceY(g2,g1) = 22
    c: Distance(g10) = 14
    c: DistanceX(g5,g-1) = 19
    c: DistanceY(g-1,g5) = 8
    c: Distance(g7) = 16
    c: Coincident(g13,g8)
    c: Vertical(g13)
    c: Coincident(g13,g11)
    c: DistanceY(g-1,g9) = 7
    c: DistanceX(g1,g9) = 8
    c: Coincident(g6,g7)
    c: Coincident(g5,g7)
    c: Coincident(g9,g14)
    c: Horizontal(g14)
    c: Coincident(g14,g15)
    c: Vertical(g15)
    c: Coincident(g15,g16)
    c: Coincident(g16,g10)
    c: Horizontal(g16)
    c: Distance(g14) = 7
    c: Coincident(g2,g17)
    c: Coincident(g0,g17)
FEATURE [PartDesign::Pad] Pad011
  Length = 2
  Length2 = 100
  Placement = pos=(0,0,11.2) rot=(0,0,1;0rad)
  Sketch = -> Sketch016
  Type = 0
FEATURE [Sketcher::SketchObject] Sketch017
  Placement = pos=(0,0,2.2) rot=(0,0,1;0rad)
  sketch-geometry (8):
    g0: Circle CenterX=-19 CenterY=8 CenterZ=0 NormalX=0 NormalY=0 NormalZ=1 Radius=1.65
    g1: Circle CenterX=-19 CenterY=-8 CenterZ=0 NormalX=0 NormalY=0 NormalZ=1 Radius=1.65
    g2: Circle CenterX=19 CenterY=8 CenterZ=0 NormalX=0 NormalY=0 NormalZ=1 Radius=1.65
    g3: Circle CenterX=19 CenterY=-8 CenterZ=0 NormalX=0 NormalY=0 NormalZ=1 Radius=1.65
    g4: LineSegment [constr] StartX=-19 StartY=8 StartZ=0 EndX=19 EndY=8 EndZ=0
    g5: LineSegment [constr] StartX=19 StartY=8 StartZ=0 EndX=19 EndY=-8 EndZ=0
    g6: LineSegment [constr] StartX=-19 StartY=-8 StartZ=0 EndX=-19 EndY=8 EndZ=0
    g7: LineSegment [constr] StartX=19 StartY=-8 StartZ=0 EndX=-19 EndY=-8 EndZ=0
  constraints (20):
    c: Coincident(g4,g0)
    c: Coincident(g4,g2)
    c: Horizontal(g4)
    c: Coincident(g4,g5)
    c: Coincident(g5,g3)
    c: Vertical(g5)
    c: Radius(g0) = 1.65
    c: Equal(g0,g1)
    c: Equal(g0,g2)
    c: Equal(g0,g3)
    c: Distance(g5) = 16
    c: Coincident(g6,g1)
    c: Coincident(g7,g3)
    c: Horizontal(g7)
    c: Vertical(g6)
    c: Coincident(g7,g1)
    c: Coincident(g0,g6)
    c: DistanceY(g1,g-1) = 8
    c: DistanceX(g1,g-1) = 19
    c: Distance(g7) = 38
FEATURE [PartDesign::Pad] Pad012
  Length = 10
  Length2 = 100
  Placement = pos=(0,0,2.2) rot=(0,0,1;0rad)
  Sketch = -> Sketch017
  Type = 0
FEATURE [Sketcher::SketchObject] Sketch019
  Placement = pos=(0,0,-7) rot=(0,0,1;0rad)
  sketch-geometry (13):
    g0: LineSegment StartX=-22 StartY=11 StartZ=0 EndX=-18 EndY=11 EndZ=0
    g1: LineSegment StartX=-18 StartY=11 StartZ=0 EndX=-14 EndY=7 EndZ=0
    g2: LineSegment StartX=-14 StartY=7 StartZ=0 EndX=14 EndY=7 EndZ=0
    g3: LineSegment StartX=14 StartY=7 StartZ=0 EndX=18 EndY=11 EndZ=0
    g4: LineSegment StartX=18 StartY=11 StartZ=0 EndX=22 EndY=11 EndZ=0
    g5: LineSegment StartX=22 StartY=11 StartZ=0 EndX=22 EndY=-11 EndZ=0
    g6: LineSegment StartX=22 StartY=-11 StartZ=0 EndX=18 EndY=-11 EndZ=0
    g7: LineSegment StartX=18 StartY=-11 StartZ=0 EndX=14 EndY=-7 EndZ=0
    g8: LineSegment StartX=14 StartY=-7 StartZ=0 EndX=-14 EndY=-7 EndZ=0
    g9: LineSegment StartX=-14 StartY=-7 StartZ=0 EndX=-18 EndY=-11 EndZ=0
    g10: LineSegment StartX=-18 StartY=-11 StartZ=0 EndX=-22 EndY=-11 EndZ=0
    g11: LineSegment StartX=-22 StartY=-11 StartZ=0 EndX=-22 EndY=11 EndZ=0
    g12: LineSegment [constr] StartX=-14 StartY=7 StartZ=0 EndX=-14 EndY=-7 EndZ=0
  constraints (38):
    c: Horizontal(g0)
    c: Coincident(g0,g1)
    c: Coincident(g1,g2)
    c: Horizontal(g2)
    c: Coincident(g2,g3)
    c: Coincident(g3,g4)
    c: Horizontal(g4)
    c: Coincident(g4,g5)
    c: Vertical(g5)
    c: Coincident(g5,g6)
    c: Horizontal(g6)
    c: Coincident(g6,g7)
    c: Coincident(g7,g8)
    c: Horizontal(g8)
    c: Coincident(g8,g9)
    c: Coincident(g9,g10)
    c: Horizontal(g10)
    c: Coincident(g10,g11)
    c: Coincident(g11,g0)
    c: Vertical(g11)
    c: Equal(g0,g10)
    c: Equal(g10,g6)
    c: Equal(g6,g4)
    c: Equal(g5,g11)
    c: Equal(g2,g8)
    c: Equal(g3,g1)
    c: Equal(g1,g9)
    c: Equal(g9,g7)
    c: Coincident(g12,g1)
    c: Coincident(g12,g8)
    c: Vertical(g12)
    c: Distance(g11) = 22
    c: DistanceX(g0,g1) = 8
    c: DistanceX(g0,g4) = 44
    c: Angle(g2,g1) = 2.35619
    c: DistanceX(g0,g-1) = 22
    c: DistanceY(g8,g-1) = 7
    c: DistanceY(g12,g12) = 14
FEATURE [PartDesign::Pad] Pad013
  Length = 18
  Length2 = 100
  Placement = pos=(0,0,-7) rot=(0,0,1;0rad)
  Sketch = -> Sketch019
  Type = 0
FEATURE [Part::Box] Box011  label="Cube010"
  Height = 3.25
  Length = 4
  Placement = pos=(-13,-2,12) rot=(0,0,1;0rad)
  Width = 4
FEATURE [Part::Box] Box012  label="Cube011"
  Height = 23
  Length = 14
  Placement = pos=(-7,-11,-8) rot=(0,0,1;0rad)
  Width = 22
FEATURE [Part::Cut] Cut008
  Base = -> Pad013
  Tool = -> Box012
FEATURE [Part::Cut] Cut009
  Base = -> Cut008
  Tool = -> Pad010
FEATURE [Part::MultiFuse] Fusion011
  Shapes = -> [Cut009,Pad009]
FEATURE [Sketcher::SketchObject] Sketch020
  Placement = pos=(0,0,-14) rot=(0,0,1;0rad)
  sketch-geometry (100):
    g0: LineSegment [constr] StartX=-36 StartY=-17.5 StartZ=0 EndX=-21.5 EndY=-27 EndZ=0
    g1: LineSegment [constr] StartX=21.5 StartY=-27 StartZ=0 EndX=36 EndY=-17.5 EndZ=0
    g2: LineSegment [constr] StartX=-36 StartY=17.5 StartZ=0 EndX=-17.7513 EndY=28 EndZ=0
    g3: LineSegment [constr] StartX=-17.7513 StartY=28 StartZ=0 EndX=-14 EndY=42 EndZ=0
    g4: LineSegment [constr] StartX=-14 StartY=42 StartZ=0 EndX=14 EndY=42 EndZ=0
    g5: LineSegment [constr] StartX=14 StartY=42 StartZ=0 EndX=17.7513 EndY=28 EndZ=0
    g6: LineSegment [constr] StartX=17.7513 StartY=28 StartZ=0 EndX=36 EndY=17.5 EndZ=0
    g7: LineSegment [constr] StartX=-21.5 StartY=-27 StartZ=0 EndX=21.5 EndY=-27 EndZ=0
    g8: LineSegment [constr] StartX=-36 StartY=17.5 StartZ=0 EndX=36 EndY=17.5 EndZ=0
    g9: LineSegment [constr] StartX=-17.7513 StartY=28 StartZ=0 EndX=17.7513 EndY=28 EndZ=0
    g10: LineSegment [constr] StartX=-36 StartY=17.5 StartZ=0 EndX=-36 EndY=15 EndZ=0
    g11: LineSegment [constr] StartX=-36 StartY=15 StartZ=0 EndX=-22 EndY=15 EndZ=0
    g12: LineSegment [constr] StartX=-22 StartY=15 StartZ=0 EndX=-22 EndY=-15 EndZ=0
    g13: LineSegment [constr] StartX=-22 StartY=-15 StartZ=0 EndX=-36 EndY=-15 EndZ=0
    g14: LineSegment [constr] StartX=-36 StartY=-15 StartZ=0 EndX=-36 EndY=-17.5 EndZ=0
    g15: LineSegment [constr] StartX=36 StartY=17.5 StartZ=0 EndX=36 EndY=15 EndZ=0
    g16: LineSegment [constr] StartX=36 StartY=15 StartZ=0 EndX=22 EndY=15 EndZ=0
    g17: LineSegment [constr] StartX=22 StartY=15 StartZ=0 EndX=22 EndY=-15 EndZ=0
    g18: LineSegment [constr] StartX=22 StartY=-15 StartZ=0 EndX=36 EndY=-15 EndZ=0
    g19: LineSegment [constr] StartX=36 StartY=-15 StartZ=0 EndX=36 EndY=-17.5 EndZ=0
    g20: LineSegment StartX=-12.9507 StartY=38.1888 StartZ=0 EndX=-15.3554 EndY=29.2143 EndZ=0
    g21: LineSegment StartX=-15.3554 StartY=29.2143 StartZ=0 EndX=-1 EndY=23.6865 EndZ=0
    g22: LineSegment StartX=-1 StartY=23.6865 StartZ=0 EndX=-1 EndY=28.2299 EndZ=0
    g23: LineSegment StartX=-1 StartY=28.2299 StartZ=0 EndX=-12.9507 EndY=38.1888 EndZ=0
    g24: LineSegment StartX=-12 StartY=40 StartZ=0 EndX=12 EndY=40 EndZ=0
    g25: LineSegment StartX=12 StartY=40 StartZ=0 EndX=0 EndY=30 EndZ=0
    g26: LineSegment StartX=0 StartY=30 StartZ=0 EndX=-12 EndY=40 EndZ=0
    g27: LineSegment StartX=1 StartY=28.2299 StartZ=0 EndX=12.9507 EndY=38.1888 EndZ=0
    g28: LineSegment StartX=12.9507 StartY=38.1888 StartZ=0 EndX=15.3554 EndY=29.2143 EndZ=0
    g29: LineSegment StartX=15.3554 StartY=29.2143 StartZ=0 EndX=1 EndY=23.6865 EndZ=0
    g30: LineSegment StartX=1 StartY=23.6865 StartZ=0 EndX=1 EndY=28.2299 EndZ=0
    g31: LineSegment StartX=1 StartY=21.5434 StartZ=0 EndX=15.3554 EndY=27.0711 EndZ=0
    g32: LineSegment StartX=15.3554 StartY=27.0711 StartZ=0 EndX=31 EndY=18.0695 EndZ=0
    g33: LineSegment StartX=31 StartY=18.0695 StartZ=0 EndX=31 EndY=17 EndZ=0
    g34: LineSegment StartX=31 StartY=17 StartZ=0 EndX=1 EndY=17 EndZ=0
    g35: LineSegment StartX=1 StartY=17 StartZ=0 EndX=1 EndY=21.5434 EndZ=0
    g36: LineSegment StartX=-15.3554 StartY=27.0711 StartZ=0 EndX=-31 EndY=18.0695 EndZ=0
    g37: LineSegment StartX=-31 StartY=17 StartZ=0 EndX=-1 EndY=17 EndZ=0
    g38: LineSegment StartX=-1 StartY=17 StartZ=0 EndX=-1 EndY=21.5434 EndZ=0
    g39: LineSegment StartX=-1 StartY=21.5434 StartZ=0 EndX=-15.3554 EndY=27.0711 EndZ=0
    g40: LineSegment StartX=-15 StartY=15 StartZ=0 EndX=-15 EndY=12.5 EndZ=0
    g41: LineSegment StartX=-15 StartY=12.5 StartZ=0 EndX=-13.5 EndY=11 EndZ=0
    g42: LineSegment StartX=-13.5 StartY=11 StartZ=0 EndX=13.5 EndY=11 EndZ=0
    g43: LineSegment StartX=13.5 StartY=11 StartZ=0 EndX=15 EndY=12.5 EndZ=0
    g44: LineSegment StartX=15 StartY=12.5 StartZ=0 EndX=15 EndY=15 EndZ=0
    g45: LineSegment StartX=15 StartY=15 StartZ=0 EndX=-15 EndY=15 EndZ=0
    g46: LineSegment StartX=-7 StartY=-25 StartZ=0 EndX=-7 EndY=-17 EndZ=0
    g47: LineSegment StartX=7 StartY=-17 StartZ=0 EndX=33.1137 EndY=-17 EndZ=0
    g48: LineSegment StartX=33.1137 StartY=-17 StartZ=0 EndX=20.9032 EndY=-25 EndZ=0
    g49: LineSegment StartX=20.9032 StartY=-25 StartZ=0 EndX=7 EndY=-25 EndZ=0
    g50: LineSegment StartX=7 StartY=-25 StartZ=0 EndX=7 EndY=-17 EndZ=0
    g51: LineSegment StartX=-5 StartY=-11 StartZ=0 EndX=-5 EndY=-25 EndZ=0
    g52: LineSegment StartX=-5 StartY=-25 StartZ=0 EndX=5 EndY=-25 EndZ=0
    g53: LineSegment StartX=5 StartY=-25 StartZ=0 EndX=5 EndY=-11 EndZ=0
    g54: LineSegment StartX=5 StartY=-11 StartZ=0 EndX=-5 EndY=-11 EndZ=0
    g55: LineSegment StartX=-5 StartY=9 StartZ=0 EndX=-5 EndY=-9 EndZ=0
    g56: LineSegment StartX=-5 StartY=-9 StartZ=0 EndX=5 EndY=-9 EndZ=0
    g57: LineSegment StartX=5 StartY=-9 StartZ=0 EndX=5 EndY=9 EndZ=0
    g58: LineSegment StartX=-33.1137 StartY=-17 StartZ=0 EndX=-7 EndY=-17 EndZ=0
    g59: LineSegment StartX=-33.1137 StartY=-17 StartZ=0 EndX=-20.9032 EndY=-25 EndZ=0
    g60: LineSegment StartX=-20.9032 StartY=-25 StartZ=0 EndX=-7 EndY=-25 EndZ=0
    g61: LineSegment StartX=-5 StartY=9 StartZ=0 EndX=5 EndY=9 EndZ=0
    g62: LineSegment [constr] StartX=-12 StartY=40 StartZ=0 EndX=-12 EndY=42 EndZ=0
    g63: LineSegment [constr] StartX=-12 StartY=40 StartZ=0 EndX=-13.2804 EndY=38.4636 EndZ=0
    g64: LineSegment [constr] StartX=12 StartY=40 StartZ=0 EndX=13.2804 EndY=38.4636 EndZ=0
    g65: LineSegment [constr] StartX=-1 StartY=28.2299 StartZ=0 EndX=1 EndY=28.2299 EndZ=0
    g66: LineSegment [constr] StartX=12.9507 StartY=38.1888 StartZ=0 EndX=14.8825 EndY=38.7064 EndZ=0
    g67: LineSegment [constr] StartX=-15.3554 StartY=29.2143 StartZ=0 EndX=15.3554 EndY=29.2143 EndZ=0
    g68: LineSegment [constr] StartX=-12.9507 StartY=38.1888 StartZ=0 EndX=-14.8825 EndY=38.7064 EndZ=0
    g69: LineSegment [constr] StartX=-1 StartY=23.6865 StartZ=0 EndX=1 EndY=23.6865 EndZ=0
    g70: LineSegment [constr] StartX=-15.3554 StartY=27.0711 StartZ=0 EndX=-16.3528 EndY=28.8047 EndZ=0
    g71: LineSegment [constr] StartX=-1 StartY=21.5434 StartZ=0 EndX=-0.281311 EndY=23.4098 EndZ=0
    g72: LineSegment [constr] StartX=-1 StartY=17 StartZ=0 EndX=1 EndY=17 EndZ=0
    g73: LineSegment [constr] StartX=1 StartY=21.5434 StartZ=0 EndX=0.281311 EndY=23.4098 EndZ=0
    g74: LineSegment [constr] StartX=31 StartY=17 StartZ=0 EndX=31 EndY=15 EndZ=0
    g75: LineSegment [constr] StartX=15.3554 StartY=27.0711 StartZ=0 EndX=16.3528 EndY=28.8047 EndZ=0
    g76: LineSegment StartX=-31 StartY=17 StartZ=0 EndX=-31 EndY=18.0695 EndZ=0
    g77: LineSegment [constr] StartX=31 StartY=17 StartZ=0 EndX=36 EndY=17 EndZ=0
    g78: LineSegment [constr] StartX=-1 StartY=17 StartZ=0 EndX=-1 EndY=15 EndZ=0
    g79: LineSegment [constr] StartX=-15 StartY=12.5 StartZ=0 EndX=15 EndY=12.5 EndZ=0
    g80: LineSegment [constr] StartX=-5 StartY=9 StartZ=0 EndX=-5 EndY=11 EndZ=0
    g81: LineSegment [constr] StartX=-5 StartY=-9 StartZ=0 EndX=-5 EndY=-11 EndZ=0
    g82: LineSegment [constr] StartX=5 StartY=-11 StartZ=0 EndX=5 EndY=-9 EndZ=0
    g83: LineSegment [constr] StartX=5 StartY=-25 StartZ=0 EndX=7 EndY=-25 EndZ=0
    g84: LineSegment [constr] StartX=-7 StartY=-25 StartZ=0 EndX=-5 EndY=-25 EndZ=0
    g85: LineSegment [constr] StartX=-5 StartY=-25 StartZ=0 EndX=-5 EndY=-27 EndZ=0
    g86: LineSegment [constr] StartX=-33.1137 StartY=-17 StartZ=0 EndX=-33.1137 EndY=-15 EndZ=0
    g87: LineSegment [constr] StartX=-33.1137 StartY=-17 StartZ=0 EndX=-34.2098 EndY=-18.6729 EndZ=0
    g88: LineSegment StartX=-16 StartY=-13 StartZ=0 EndX=-14 EndY=-11 EndZ=0
    g89: LineSegment StartX=-14 StartY=-11 StartZ=0 EndX=-7 EndY=-11 EndZ=0
    g90: LineSegment StartX=-7 StartY=-11 StartZ=0 EndX=-7 EndY=-15 EndZ=0
    g91: LineSegment StartX=-7 StartY=-15 StartZ=0 EndX=-16 EndY=-15 EndZ=0
    g92: LineSegment StartX=-16 StartY=-15 StartZ=0 EndX=-16 EndY=-13 EndZ=0
    g93: LineSegment StartX=7 StartY=-11 StartZ=0 EndX=14 EndY=-11 EndZ=0
    g94: LineSegment StartX=14 StartY=-11 StartZ=0 EndX=16 EndY=-13 EndZ=0
    g95: LineSegment StartX=16 StartY=-13 StartZ=0 EndX=16 EndY=-15 EndZ=0
    g96: LineSegment StartX=16 StartY=-15 StartZ=0 EndX=7 EndY=-15 EndZ=0
    g97: LineSegment StartX=7 StartY=-15 StartZ=0 EndX=7 EndY=-11 EndZ=0
    g98: LineSegment [constr] StartX=7 StartY=-15 StartZ=0 EndX=7 EndY=-17 EndZ=0
    g99: LineSegment [constr] StartX=-7 StartY=-15 StartZ=0 EndX=-7 EndY=-17 EndZ=0
  constraints (287):
    c: Coincident(g2,g3)
    c: Coincident(g3,g4)
    c: Horizontal(g4)
    c: Coincident(g4,g5)
    c: Coincident(g5,g6)
    c: Equal(g1,g0)
    c: DistanceX(g0,g1) = 72
    c: Equal(g2,g6)
    c: Horizontal(g8)
    c: Equal(g3,g5)
    c: DistanceX(g2,g-1) = 36
    c: Distance(g4) = 28
    c: DistanceY(g-1,g2) = 17.5
    c: DistanceY(g-1,g5) = 28
    c: Angle(g3,g4) = 1.8326
    c: Coincident(g9,g2)
    c: Coincident(g9,g5)
    c: Horizontal(g9)
    c: Coincident(g1,g7)
    c: Coincident(g0,g7)
    c: Horizontal(g7)
    c: DistanceY(g-1,g3) = 42
    c: Distance(g7) = 43
    c: DistanceY(g1,g4) = 69
    c: DistanceY(g0,g2) = 35
    c: Coincident(g2,g10)
    c: Vertical(g10)
    c: Coincident(g10,g11)
    c: Horizontal(g11)
    c: Coincident(g11,g12)
    c: Vertical(g12)
    c: Coincident(g12,g13)
    c: Horizontal(g13)
    c: Coincident(g13,g14)
    c: Coincident(g14,g0)
    c: Vertical(g14)
    c: Equal(g10,g14)
    c: Distance(g12) = 30
    c: Distance(g11) = 14
    c: Coincident(g6,g15)
    c: Vertical(g15)
    c: Coincident(g15,g16)
    c: Horizontal(g16)
    c: Coincident(g16,g17)
    c: Vertical(g17)
    c: Coincident(g17,g18)
    c: Coincident(g18,g19)
    c: Vertical(g19)
    c: Coincident(g1,g19)
    c: Horizontal(g18)
    c: Equal(g14,g15)
    c: Equal(g15,g19)
    c: Equal(g17,g12)
    c: Equal(g13,g18)
    c: Equal(g16,g11)
    c: Equal(g16,g18)
    c: Coincident(g8,g6)
    c: Coincident(g8,g2)
    c: Coincident(g20,g21)
    c: Coincident(g21,g22)
    c: Vertical(g22)
    c: Coincident(g22,g23)
    c: Coincident(g23,g20)
    c: Horizontal(g24)
    c: Coincident(g24,g25)
    c: Coincident(g25,g26)
    c: Coincident(g26,g24)
    c: Coincident(g27,g28)
    c: Coincident(g28,g29)
    c: Coincident(g29,g30)
    c: Coincident(g30,g27)
    c: Vertical(g30)
    c: Coincident(g31,g32)
    c: Coincident(g32,g33)
    c: Vertical(g33)
    c: Coincident(g33,g34)
    c: Coincident(g34,g35)
    c: Coincident(g35,g31)
    c: Horizontal(g37)
    c: Coincident(g37,g38)
    c: Coincident(g38,g39)
    c: Coincident(g39,g36)
    c: Coincident(g40,g41)
    c: Coincident(g41,g42)
    c: Horizontal(g42)
    c: Coincident(g42,g43)
    c: Coincident(g43,g44)
    c: Coincident(g44,g45)
    c: Horizontal(g45)
    c: Coincident(g40,g45)
    c: Horizontal(g47)
    c: Coincident(g47,g48)
    c: Coincident(g48,g49)
    c: Horizontal(g49)
    c: Coincident(g49,g50)
    c: Coincident(g50,g47)
    c: Coincident(g51,g52)
    c: Coincident(g52,g53)
    c: Coincident(g53,g54)
    c: Horizontal(g54)
    c: Vertical(g55)
    c: Coincident(g55,g56)
    c: Horizontal(g56)
    c: Coincident(g56,g57)
    c: Vertical(g57)
    c: Coincident(g58,g46)
    c: Coincident(g58,g59)
    c: Coincident(g59,g60)
    c: Coincident(g60,g46)
    c: Coincident(g51,g54)
    c: Vertical(g51)
    c: Vertical(g53)
    c: Horizontal(g52)
    c: Vertical(g46)
    c: Vertical(g50)
    c: Horizontal(g60)
    c: Horizontal(g58)
    c: Coincident(g61,g55)
    c: Coincident(g61,g57)
    c: Horizontal(g61)
    c: Vertical(g40)
    c: Vertical(g44)
    c: Angle(g43,g42) = 2.35619
    c: Vertical(g38)
    c: Vertical(g35)
    c: Horizontal(g34)
    c: PointOnObject(g25,g-2)
    c: PointOnObject(g62,g4)
    c: Vertical(g62)
    c: Coincident(g24,g62)
    c: Symmetric(g24,g24,g-2)
    c: Coincident(g63,g24)
    c: PointOnObject(g63,g23)
    c: Perpendicular(g23,g63)
    c: Coincident(g64,g24)
    c: PointOnObject(g64,g27)
    c: Perpendicular(g27,g64)
    c: Coincident(g65,g22)
    c: Coincident(g65,g27)
    c: Horizontal(g65)
    c: Parallel(g23,g26)
    c: Parallel(g25,g27)
    c: Equal(g28,g20)
    c: Coincident(g66,g27)
    c: PointOnObject(g66,g5)
    c: Perpendicular(g5,g66)
    c: Equal(g63,g62)
    c: Equal(g62,g66)
    c: Equal(g66,g64)
    c: Coincident(g67,g20)
    c: Coincident(g67,g28)
    c: Horizontal(g67)
    c: Equal(g66,g65)
    c: Coincident(g68,g20)
    c: PointOnObject(g68,g3)
    c: Perpendicular(g68,g3)
    c: Parallel(g31,g29)
    c: Parallel(g39,g21)
    c: Coincident(g69,g21)
    c: Coincident(g29,g69)
    c: Horizontal(g69)
    c: Parallel(g28,g5)
    c: Parallel(g36,g2)
    c: Parallel(g3,g20)
    c: Coincident(g70,g36)
    c: PointOnObject(g70,g2)
    c: Perpendicular(g70,g2)
    c: Equal(g70,g65)
    c: Parallel(g32,g6)
    c: Coincident(g71,g38)
    c: PointOnObject(g71,g21)
    c: Perpendicular(g21,g71)
    c: Equal(g71,g65)
    c: Equal(g38,g35)
    c: Coincident(g34,g72)
    c: Coincident(g37,g72)
    c: Horizontal(g72)
    c: Coincident(g73,g31)
    c: PointOnObject(g73,g29)
    c: Equal(g73,g71)
    c: Perpendicular(g29,g73)
    c: Equal(g72,g69)
    c: Coincident(g74,g33)
    c: PointOnObject(g74,g16)
    c: Vertical(g74)
    c: Equal(g74,g73)
    c: PointOnObject(g75,g6)
    c: Coincident(g31,g75)
    c: Perpendicular(g6,g75)
    c: Equal(g75,g69)
    c: Coincident(g76,g37)
    c: Coincident(g76,g36)
    c: Vertical(g76)
    c: Equal(g33,g76)
    c: Coincident(g77,g33)
    c: PointOnObject(g77,g15)
    c: Horizontal(g77)
    c: Distance(g77) = 5
    c: Coincident(g78,g37)
    c: PointOnObject(g78,g45)
    c: Vertical(g78)
    c: Equal(g78,g72)
    c: Distance(g68) = 2
    c: Coincident(g79,g40)
    c: Coincident(g79,g43)
    c: Horizontal(g79)
    c: Symmetric(g40,g44,g-2)
    c: Equal(g41,g43)
    c: Distance(g45) = 30
    c: Distance(g40) = 2.5
    c: DistanceY(g42,g44) = 4
    c: Symmetric(g57,g55,g-2)
    c: Coincident(g80,g55)
    c: PointOnObject(g80,g42)
    c: Vertical(g80)
    c: Equal(g80,g74)
    c: Distance(g56) = 10
    c: Coincident(g81,g55)
    c: Vertical(g81)
    c: Coincident(g51,g81)
    c: Coincident(g56,g82)
    c: Coincident(g53,g82)
    c: Vertical(g82)
    c: Equal(g80,g81)
    c: Distance(g55) = 18
    c: Coincident(g83,g52)
    c: Coincident(g83,g49)
    c: Horizontal(g83)
    c: Coincident(g84,g46)
    c: Coincident(g84,g51)
    c: Horizontal(g84)
    c: Equal(g84,g83)
    c: Equal(g83,g81)
    c: Parallel(g59,g0)
    c: Coincident(g85,g51)
    c: PointOnObject(g85,g7)
    c: Vertical(g85)
    c: Equal(g85,g84)
    c: Coincident(g86,g58)
    c: PointOnObject(g86,g13)
    c: Vertical(g86)
    c: Coincident(g87,g58)
    c: PointOnObject(g87,g0)
    c: Equal(g86,g87)
    c: Equal(g87,g84)
    c: Perpendicular(g0,g87)
    c: Equal(g50,g46)
    c: Parallel(g48,g1)
    c: Equal(g49,g60)
    c: Distance(g24) = 24
    c: DistanceY(g-1,g25) = 30
    c: Equal(g30,g35)
    c: Equal(g29,g31)
    c: Coincident(g88,g89)
    c: Horizontal(g89)
    c: Coincident(g89,g90)
    c: Vertical(g90)
    c: Coincident(g90,g91)
    c: Coincident(g91,g92)
    c: Coincident(g92,g88)
    c: Vertical(g92)
    c: Horizontal(g93)
    c: Coincident(g93,g94)
    c: Coincident(g94,g95)
    c: Vertical(g95)
    c: Coincident(g95,g96)
    c: Horizontal(g96)
    c: Coincident(g96,g97)
    c: Vertical(g97)
    c: Coincident(g93,g97)
    c: Horizontal(g91)
    c: Angle(g88,g89) = 2.35619
    c: Angle(g93,g94) = 2.35619
    c: Equal(g89,g93)
    c: Vertical(g98)
    c: Coincident(g96,g98)
    c: Coincident(g47,g98)
    c: Vertical(g99)
    c: Coincident(g90,g99)
    c: Coincident(g46,g99)
    c: Equal(g99,g98)
    c: Equal(g98,g82)
    c: Equal(g90,g97)
    c: Distance(g91) = 9
    c: Equal(g92,g95)
    c: DistanceY(g97,g97) = 4
    c: Distance(g95) = 2
FEATURE [PartDesign::Pad] Pad014
  Length = 20
  Length2 = 100
  Placement = pos=(0,0,-14) rot=(0,0,1;0rad)
  Sketch = -> Sketch020
  Type = 0
FEATURE [Part::Fillet] Fillet009
  Base = -> Pad014
  Edges = 159 edges r=0.6: [Edge1,Edge2,Edge3,Edge4,Edge5,Edge6,Edge7,Edge8,Edge9,Edge10,Edge11,Edge12,Edge13,Edge14,Edge15,Edge16,Edge17,Edge18,Edge19,Edge20,Edge21,Edge22,Edge23,Edge24,Edge25,Edge26,Edge27,Edge28,Edge29,Edge30,Edge31,Edge32,Edge33,Edge34,Edge35,Edge36,Edge37,Edge38,Edge39,Edge40,Edge41,Edge42,Edge43,Edge44,+115 more]
FEATURE [Part::Fillet] Fillet001
  Base = -> Box001
  Edges = 12 edges r=1.5: [Edge1,Edge2,Edge3,Edge4,Edge5,Edge6,Edge7,Edge8,Edge9,Edge10,Edge11,Edge12]
  Placement = pos=(-22,-27,-5) rot=(0,0,1;0rad)
FEATURE [Part::Cut] Cut010
  Base = -> Fusion011
  Tool = -> Pad012
FEATURE [Sketcher::SketchObject] Sketch021
  Placement = pos=(0,0,15) rot=(0,0,1;0rad)
  sketch-geometry (7):
    g0: LineSegment StartX=22 StartY=-26 StartZ=0 EndX=-22 EndY=-26 EndZ=0
    g1: LineSegment StartX=-16.5 StartY=27.5 StartZ=0 EndX=15 EndY=27.5 EndZ=0
    g2: LineSegment StartX=-22 StartY=11 StartZ=0 EndX=-16.5 EndY=11 EndZ=0
    g3: LineSegment StartX=-16.5 StartY=27.5 StartZ=0 EndX=-16.5 EndY=11 EndZ=0
    g4: LineSegment StartX=15 StartY=27.5 StartZ=0 EndX=22 EndY=15 EndZ=0
    g5: LineSegment StartX=-22 StartY=11 StartZ=0 EndX=-22 EndY=-26 EndZ=0
    g6: LineSegment StartX=22 StartY=15 StartZ=0 EndX=22 EndY=-26 EndZ=0
  constraints (21):
    c: Horizontal(g0)
    c: Horizontal(g1)
    c: DistanceY(g0,g1) = 53.5
    c: Horizontal(g2)
    c: Coincident(g3,g1)
    c: Coincident(g3,g2)
    c: Coincident(g4,g1)
    c: Vertical(g3)
    c: DistanceY(g3,g3) = 16.5
    c: Distance(g1) = 31.5
    c: Distance(g2) = 5.5
    c: Coincident(g2,g5)
    c: Vertical(g5)
    c: DistanceX(g2,g-1) = 22
    c: Vertical(g6)
    c: Coincident(g4,g6)
    c: DistanceY(g-1,g4) = 15
    c: Coincident(g0,g5)
    c: Coincident(g0,g6)
    c: Distance(g0) = 44
    c: DistanceY(g-1,g1) = 27.5
FEATURE [PartDesign::Pad] Pad015
  Length = 1.2
  Length2 = 100
  Placement = pos=(0,0,15) rot=(0,0,1;0rad)
  Sketch = -> Sketch021
  Type = 0
FEATURE [Part::Cylinder] Cylinder023
  Angle = 360
  Height = 20
  Radius = 0.5
FEATURE [Part::FeaturePython] Array001  # Draft array (typed FeaturePython)
  Angle = 360
  ArrayType = 0
  Axis = (0,0,1)
  Base = -> Cylinder023
  Center = (0,0,0)
  Fuse = false
  IntervalAxis = (0,0,0)
  IntervalX = (2.54,0,0)
  IntervalY = (0,2.54,0)
  IntervalZ = (0,0,0)
  NumberPolar = 1
  NumberX = 17
  NumberY = 21
  NumberZ = 1
  Placement = pos=(-20.3,-24.8,0) rot=(0,0,1;0rad)
FEATURE [Part::Cut] Cut011  label="pcb"
  Base = -> Pad015
  Placement = pos=(0,-1,0) rot=(0,0,1;0rad)
  Tool = -> Array001
FEATURE [Sketcher::SketchObject] Sketch022
  Placement = pos=(0,0,-6) rot=(0,0,1;0rad)
  sketch-geometry (5):
    g0: LineSegment StartX=-22.5 StartY=-15.5 StartZ=0 EndX=-22.5 EndY=-21 EndZ=0
    g1: LineSegment StartX=-22.5 StartY=-21 StartZ=0 EndX=-28.75 EndY=-21 EndZ=0
    g2: LineSegment StartX=-33.5 StartY=-16.9 StartZ=0 EndX=-33.5 EndY=-15.5 EndZ=0
    g3: LineSegment StartX=-33.5 StartY=-15.5 StartZ=0 EndX=-22.5 EndY=-15.5 EndZ=0
    g4: LineSegment StartX=-33.5 StartY=-16.9 StartZ=0 EndX=-28.75 EndY=-21 EndZ=0
  constraints (15):
    c: Coincident(g0,g1)
    c: Horizontal(g1)
    c: Vertical(g0)
    c: DistanceY(g0,g-1) = 15.5
    c: Distance(g0) = 5.5
    c: Vertical(g2)
    c: Coincident(g3,g2)
    c: Coincident(g3,g0)
    c: Horizontal(g3)
    c: Coincident(g4,g2)
    c: Coincident(g4,g1)
    c: Distance(g3) = 11
    c: DistanceX(g2,g-1) = 33.5
    c: Distance(g1) = 6.25
    c: Distance(g2) = 1.4
FEATURE [PartDesign::Pad] Pad016
  Length = 31
  Length2 = 100
  Placement = pos=(0,0,-6) rot=(0,0,1;0rad)
  Sketch = -> Sketch022
  Type = 0
FEATURE [Part::Cylinder] Cylinder024
  Angle = 360
  Height = 10
  Placement = pos=(-26,-18,19.5) rot=(0,0,1;0rad)
  Radius = 1.65
FEATURE [Part::Cut] Cut012
  Base = -> Pad016
  Tool = -> Cylinder024
FEATURE [Part::Mirroring] Part__Mirroring001  label="Cut012 (Mirror #2)"
  Base = (0,0,0)
  Normal = (1,0,0)
  Source = -> Cut012
FEATURE [Part::MultiFuse] Fusion012
  Shapes = -> [Cut012,Part__Mirroring001]
FEATURE [Part::MultiFuse] Fusion013
  Shapes = -> [Fusion012,Cut010]
FEATURE [Sketcher::SketchObject] Sketch023
  Placement = pos=(-11,-27.5,25) rot=(0,0,1;0rad)
  Support = -> Box002 [Face6]
FEATURE [Sketcher::SketchObject] Sketch024
  Placement = pos=(0,0,-4.75) rot=(0,0,1;0rad)
  sketch-geometry (21):
    g0: LineSegment StartX=-36 StartY=-15.5 StartZ=0 EndX=-34 EndY=-15.5 EndZ=0
    g1: LineSegment StartX=-34 StartY=-15.5 StartZ=0 EndX=-34 EndY=-17.133 EndZ=0
    g2: LineSegment StartX=-22.5 StartY=-27.5 StartZ=0 EndX=22.5 EndY=-27.5 EndZ=0
    g3: LineSegment StartX=34 StartY=-17.133 StartZ=0 EndX=34 EndY=-15.5 EndZ=0
    g4: LineSegment StartX=34 StartY=-15.5 StartZ=0 EndX=36 EndY=-15.5 EndZ=0
    g5: LineSegment StartX=36 StartY=-15.5 StartZ=0 EndX=36 EndY=-17.5 EndZ=0
    g6: LineSegment StartX=36 StartY=-17.5 StartZ=0 EndX=23 EndY=-29 EndZ=0
    g7: LineSegment StartX=23 StartY=-29 StartZ=0 EndX=-23 EndY=-29 EndZ=0
    g8: LineSegment StartX=-23 StartY=-29 StartZ=0 EndX=-36 EndY=-17.5 EndZ=0
    g9: LineSegment StartX=-36 StartY=-17.5 StartZ=0 EndX=-36 EndY=-15.5 EndZ=0
    g10: LineSegment [constr] StartX=-34 StartY=-15.5 StartZ=0 EndX=34 EndY=-15.5 EndZ=0
    g11: LineSegment StartX=-22.5 StartY=-27.5 StartZ=0 EndX=-22.5 EndY=-21.7773 EndZ=0
    g12: LineSegment StartX=-22.5 StartY=-21.7773 StartZ=0 EndX=-28.75 EndY=-21.7773 EndZ=0
    g13: LineSegment StartX=-34 StartY=-17.133 StartZ=0 EndX=-28.75 EndY=-21.7773 EndZ=0
    g14: LineSegment StartX=34 StartY=-17.133 StartZ=0 EndX=28.75 EndY=-21.7773 EndZ=0
    g15: LineSegment StartX=28.75 StartY=-21.7773 StartZ=0 EndX=22.5 EndY=-21.7773 EndZ=0
    g16: LineSegment StartX=22.5 StartY=-21.7773 StartZ=0 EndX=22.5 EndY=-27.5 EndZ=0
    g17: LineSegment [constr] StartX=-22.5 StartY=-21.7773 StartZ=0 EndX=22.5 EndY=-21.7773 EndZ=0
    g18: LineSegment [constr] StartX=-22.5 StartY=-27.5 StartZ=0 EndX=-22.5 EndY=-29 EndZ=0
    g19: LineSegment [constr] StartX=-28.75 StartY=-21.7773 StartZ=0 EndX=-29.8101 EndY=-22.9757 EndZ=0
    g20: LineSegment [constr] StartX=28.75 StartY=-21.7773 StartZ=0 EndX=29.8101 EndY=-22.9757 EndZ=0
  constraints (61):
    c: Coincident(g0,g1)
    c: Vertical(g1)
    c: Coincident(g4,g5)
    c: Coincident(g5,g6)
    c: Distance(g7) = 46
    c: Vertical(g5)
    c: Vertical(g3)
    c: Equal(g8,g6)
    c: Equal(g1,g3)
    c: DistanceX(g0,g4) = 72
    c: DistanceY(g0,g-1) = 15.5
    c: Coincident(g11,g12)
    c: Horizontal(g12)
    c: Coincident(g13,g1)
    c: Coincident(g13,g12)
    c: Coincident(g3,g14)
    c: Coincident(g14,g15)
    c: Horizontal(g15)
    c: Coincident(g15,g16)
    c: Vertical(g16)
    c: Distance(g12) = 6.25
    c: Equal(g12,g15)
    c: Parallel(g14,g6)
    c: Coincident(g17,g11)
    c: Horizontal(g17)
    c: Coincident(g15,g17)
    c: Coincident(g2,g16)
    c: Coincident(g2,g11)
    c: Vertical(g11)
    c: DistanceX(g11,g-1) = 22.5
    c: Horizontal(g0)
    c: Parallel(g13,g8)
    c: DistanceX(g0,g0) = 2
    c: Coincident(g0,g9)
    c: Vertical(g9)
    c: Coincident(g8,g9)
    c: Coincident(g3,g4)
    c: Coincident(g3,g10)
    c: Horizontal(g4)
    c: Equal(g0,g4)
    c: Coincident(g6,g7)
    c: Coincident(g7,g8)
    c: Horizontal(g2)
    c: Horizontal(g7)
    c: Coincident(g18,g2)
    c: PointOnObject(g18,g7)
    c: Vertical(g18)
    c: Coincident(g19,g12)
    c: PointOnObject(g19,g8)
    c: Perpendicular(g8,g19)
    c: PointOnObject(g20,g6)
    c: Perpendicular(g6,g20)
    c: Coincident(g14,g20)
    c: Distance(g2) = 45
    c: Distance(g9) = 2
    c: DistanceY(g7,g0) = 13.5
    c: Coincident(g10,g0)
    c: Horizontal(g10)
    c: Distance(g18) = 1.5
    c: Equal(g19,g20)
    c: Distance(g19) = 1.6
FEATURE [PartDesign::Pad] Pad017
  Length = 29.5
  Length2 = 100
  Placement = pos=(0,0,-4.75) rot=(0,0,1;0rad)
  Sketch = -> Sketch024
  Type = 0
FEATURE [Part::Cylinder] Cylinder025
  Angle = 360
  Height = 14
  Placement = pos=(-26,-17,5) rot=(1,0,0;1.5708rad)
  Radius = 1.1
FEATURE [Part::Cylinder] Cylinder026
  Angle = 360
  Height = 14
  Placement = pos=(26,-17,5) rot=(1,0,0;1.5708rad)
  Radius = 1.1
FEATURE [Part::MultiFuse] Fusion014
  Placement = pos=(0,0,-9.75) rot=(0,0,1;0rad)
  Shapes = -> [Cylinder025,Cylinder026]
FEATURE [Part::MultiFuse] Fusion015
  Placement = pos=(0,0,5) rot=(0,0,1;0rad)
  Shapes = -> [Cylinder025,Cylinder026]
FEATURE [Part::Cut] Cut014
  Base = -> Fusion013
  Tool = -> Fusion015
FEATURE [Part::Cylinder] Cylinder027
  Angle = 360
  Height = 14
  Placement = pos=(-26,-17,-4.75) rot=(1,0,0;1.5708rad)
  Radius = 2.5
FEATURE [Part::Cylinder] Cylinder028
  Angle = 360
  Height = 14
  Placement = pos=(26,-17,-4.75) rot=(1,0,0;1.5708rad)
  Radius = 2.5
FEATURE [Part::MultiFuse] Fusion016
  Placement = pos=(0,-7,0) rot=(0,0,1;0rad)
  Shapes = -> [Cylinder027,Cylinder028]
FEATURE [Part::MultiFuse] Fusion017
  Placement = pos=(0,0,14.75) rot=(0,0,1;0rad)
  Shapes = -> [Fusion016,Fusion014]
FEATURE [Part::Cut] Cut015
  Base = -> Pad017
  Tool = -> Fusion017
FEATURE [Part::Cylinder] Cylinder029
  Angle = 360
  Height = 30
  Placement = pos=(0,0,-10) rot=(0,0,1;0rad)
  Radius = 1.5
FEATURE [Part::Cylinder] Cylinder030
  Angle = 360
  Height = 30
  Placement = pos=(6,0,-10) rot=(0,0,1;0rad)
  Radius = 1.8
FEATURE [Part::FeaturePython] Array  # Draft array (typed FeaturePython)
  Angle = 360
  ArrayType = 1
  Axis = (0,0,1)
  Base = -> Cylinder030
  Center = (0,0,0)
  Fuse = false
  IntervalAxis = (0,0,0)
  IntervalX = (1,0,0)
  IntervalY = (0,1,0)
  IntervalZ = (0,0,0)
  NumberPolar = 8
  NumberX = 2
  NumberY = 2
  NumberZ = 1
FEATURE [Part::MultiFuse] Fusion018
  Shapes = -> [Cylinder029,Array]
FEATURE [Part::Cut] Cut016  label="wheel-src"
  Base = -> Cut001
  Tool = -> Fusion018
FEATURE [Part::Fillet] Fillet010
  Base = -> Cut015
  Edges = 2 edges r=0.5: [Edge51,Edge52]
FEATURE [Part::Feature] Chamfer055  label="ISO-10642-M3x012"
  Placement = pos=(-19,8,13.5) rot=(0,0,1;0rad)
  shape: bbox 6.046 x 6.046 x 10 mm, 25 faces (baked)
FEATURE [Part::Feature] Chamfer056  label="ISO-10642-M3x013"
  Placement = pos=(-19,-8,13.5) rot=(0,0,1;0rad)
  shape: bbox 6.046 x 6.046 x 10 mm, 25 faces (baked)
FEATURE [Part::Feature] Chamfer057  label="ISO-10642-M3x014"
  Placement = pos=(19,8,13.5) rot=(0,0,1;0rad)
  shape: bbox 6.046 x 6.046 x 10 mm, 25 faces (baked)
FEATURE [Part::Feature] Chamfer058  label="ISO-10642-M3x015"
  Placement = pos=(19,-8,13.5) rot=(0,0,1;0rad)
  shape: bbox 6.046 x 6.046 x 10 mm, 25 faces (baked)
FEATURE [Part::Cylinder] Cylinder031
  Angle = 360
  Height = 19
  Placement = pos=(0,0,5) rot=(0,0,1;0rad)
  Radius = 1.6
FEATURE [Part::Cylinder] Cylinder032
  Angle = 360
  Height = 21
  Placement = pos=(0,0,-6) rot=(0,0,1;0rad)
  Radius = 3.5
FEATURE [Part::Cut] Cut017
  Base = -> Cylinder032
  Tool = -> Cylinder031
FEATURE [Part::Box] Box013  label="Cube012"
  Height = 19.7
  Length = 8.5
  Placement = pos=(23.15,-3,-0.85) rot=(0,0,1;0rad)
  Width = 46
FEATURE [Part::Cut] Cut018
  Base = -> Fillet007
  Tool = -> Box013
FEATURE [Sketcher::SketchObject] Sketch025
  Placement = pos=(0,0,40) rot=(0,0,1;0rad)
  sketch-geometry (22):
    g0: LineSegment StartX=-36 StartY=-17.5 StartZ=0 EndX=-23 EndY=-29 EndZ=0
    g1: LineSegment StartX=23 StartY=-29 StartZ=0 EndX=36 EndY=-17.5 EndZ=0
    g2: LineSegment StartX=-36 StartY=17.5 StartZ=0 EndX=-17.7513 EndY=28 EndZ=0
    g3: LineSegment StartX=-17.7513 StartY=28 StartZ=0 EndX=-11.8564 EndY=50 EndZ=0
    g4: LineSegment StartX=-11.8564 StartY=50 StartZ=0 EndX=11.8564 EndY=50 EndZ=0
    g5: LineSegment StartX=11.8564 StartY=50 StartZ=0 EndX=17.7513 EndY=28 EndZ=0
    g6: LineSegment StartX=17.7513 StartY=28 StartZ=0 EndX=36 EndY=17.5 EndZ=0
    g7: LineSegment StartX=-23 StartY=-29 StartZ=0 EndX=23 EndY=-29 EndZ=0
    g8: LineSegment [constr] StartX=-36 StartY=17.5 StartZ=0 EndX=36 EndY=17.5 EndZ=0
    g9: LineSegment [constr] StartX=-17.7513 StartY=28 StartZ=0 EndX=17.7513 EndY=28 EndZ=0
    g10: LineSegment StartX=-36 StartY=17.5 StartZ=0 EndX=-36 EndY=15.5 EndZ=0
    g11: LineSegment [constr] StartX=-36 StartY=15.5 StartZ=0 EndX=-22 EndY=15.5 EndZ=0
    g12: LineSegment [constr] StartX=-22 StartY=15.5 StartZ=0 EndX=-22 EndY=-15.5 EndZ=0
    g13: LineSegment [constr] StartX=-22 StartY=-15.5 StartZ=0 EndX=-36 EndY=-15.5 EndZ=0
    g14: LineSegment StartX=-36 StartY=-15.5 StartZ=0 EndX=-36 EndY=-17.5 EndZ=0
    g15: LineSegment StartX=36 StartY=17.5 StartZ=0 EndX=36 EndY=15.5 EndZ=0
    g16: LineSegment [constr] StartX=36 StartY=15.5 StartZ=0 EndX=22 EndY=15.5 EndZ=0
    g17: LineSegment [constr] StartX=22 StartY=15.5 StartZ=0 EndX=22 EndY=-15.5 EndZ=0
    g18: LineSegment [constr] StartX=22 StartY=-15.5 StartZ=0 EndX=36 EndY=-15.5 EndZ=0
    g19: LineSegment StartX=36 StartY=-15.5 StartZ=0 EndX=36 EndY=-17.5 EndZ=0
    g20: LineSegment StartX=-36 StartY=15.5 StartZ=0 EndX=-36 EndY=-15.5 EndZ=0
    g21: LineSegment StartX=36 StartY=15.5 StartZ=0 EndX=36 EndY=-15.5 EndZ=0
  constraints (62):
    c: Coincident(g2,g3)
    c: Coincident(g3,g4)
    c: Horizontal(g4)
    c: Coincident(g4,g5)
    c: Coincident(g5,g6)
    c: Equal(g1,g0)
    c: DistanceX(g0,g1) = 72
    c: Equal(g2,g6)
    c: Horizontal(g8)
    c: Equal(g3,g5)
    c: DistanceX(g2,g-1) = 36
    c: DistanceY(g-1,g2) = 17.5
    c: DistanceY(g-1,g5) = 28
    c: Angle(g3,g4) = 1.8326
    c: Coincident(g9,g2)
    c: Coincident(g9,g5)
    c: Horizontal(g9)
    c: Coincident(g1,g7)
    c: Coincident(g0,g7)
    c: Horizontal(g7)
    c: DistanceY(g-1,g3) = 50
    c: Distance(g7) = 46
    c: DistanceY(g1,g4) = 79
    c: DistanceY(g0,g2) = 35
    c: Coincident(g2,g10)
    c: Vertical(g10)
    c: Coincident(g10,g11)
    c: Horizontal(g11)
    c: Coincident(g11,g12)
    c: Vertical(g12)
    c: Coincident(g12,g13)
    c: Horizontal(g13)
    c: Coincident(g13,g14)
    c: Coincident(g14,g0)
    c: Vertical(g14)
    c: Equal(g10,g14)
    c: Distance(g12) = 31
    c: Distance(g11) = 14
    c: Coincident(g6,g15)
    c: Vertical(g15)
    c: Coincident(g15,g16)
    c: Horizontal(g16)
    c: Coincident(g16,g17)
    c: Vertical(g17)
    c: Coincident(g17,g18)
    c: Coincident(g18,g19)
    c: Vertical(g19)
    c: Coincident(g1,g19)
    c: Horizontal(g18)
    c: Equal(g14,g15)
    c: Equal(g15,g19)
    c: Equal(g17,g12)
    c: Equal(g13,g18)
    c: Equal(g16,g11)
    c: Equal(g16,g18)
    c: Coincident(g8,g6)
    c: Coincident(g8,g2)
    c: Coincident(g20,g10)
    c: Coincident(g20,g13)
    c: Coincident(g21,g15)
    c: Coincident(g21,g18)
    c: Distance(g9) = 35.5026
FEATURE [PartDesign::Pad] Pad
  Length = 50
  Length2 = 100
  Placement = pos=(0,0,40) rot=(0,0,1;0rad)
  Reversed = true
  Sketch = -> Sketch025
  Type = 0
FEATURE [Part::MultiCommon] Common
  Shapes = -> [Pad,Pad004]
FEATURE [Part::Mirroring] Part__Mirroring002  label="Pad006 (Mirror #3)"
  Base = (0,0,0)
  Normal = (1,0,0)
  Source = -> Pad006
FEATURE [Part::MultiFuse] Fusion020
  Shapes = -> [Part__Mirroring002,Pad006]
FEATURE [Part::Cut] Cut019
  Base = -> Common
  Tool = -> Fusion020
FEATURE [Sketcher::SketchObject] Sketch028
  Placement = pos=(-50,0,0) rot=(0.57735,0.57735,0.57735;2.0944rad)
  sketch-geometry (6):
    g0: LineSegment StartX=-35 StartY=25.25 StartZ=0 EndX=-15 EndY=25.25 EndZ=0
    g1: LineSegment StartX=-15 StartY=25.25 StartZ=0 EndX=-15 EndY=-4.5 EndZ=0
    g2: LineSegment StartX=-15 StartY=-4.5 StartZ=0 EndX=41.75 EndY=-4.5 EndZ=0
    g3: LineSegment StartX=41.75 StartY=-4.5 StartZ=0 EndX=41.75 EndY=-16.5 EndZ=0
    g4: LineSegment StartX=41.75 StartY=-16.5 StartZ=0 EndX=-35 EndY=-16.5 EndZ=0
    g5: LineSegment StartX=-35 StartY=-16.5 StartZ=0 EndX=-35 EndY=25.25 EndZ=0
  constraints (18):
    c: Horizontal(g0)
    c: Coincident(g0,g1)
    c: Vertical(g1)
    c: Coincident(g1,g2)
    c: Horizontal(g2)
    c: Coincident(g2,g3)
    c: Vertical(g3)
    c: Coincident(g3,g4)
    c: Horizontal(g4)
    c: Coincident(g4,g5)
    c: Coincident(g5,g0)
    c: Vertical(g5)
    c: DistanceY(g2,g-1) = 4.5
    c: DistanceX(g-1,g2) = 41.75
    c: Distance(g3) = 12
    c: DistanceX(g1,g-1) = 15
    c: DistanceY(g-1,g0) = 25.25
    c: Distance(g0) = 20
FEATURE [PartDesign::Pad] Pad018
  Length = 100
  Length2 = 100
  Placement = pos=(-50,0,0) rot=(0.57735,0.57735,0.57735;2.0944rad)
  Sketch = -> Sketch028
  Type = 0
FEATURE [Part::Cut] Cut020
  Base = -> Cut019
  Tool = -> Pad018
FEATURE [Sketcher::SketchObject] Sketch031
  Placement = pos=(0,0,40) rot=(0,0,1;0rad)
  sketch-geometry (22):
    g0: LineSegment StartX=-34 StartY=-15.5 StartZ=0 EndX=-23 EndY=-29 EndZ=0
    g1: LineSegment StartX=23 StartY=-29 StartZ=0 EndX=34 EndY=-15.5 EndZ=0
    g2: LineSegment StartX=-34 StartY=17.5 StartZ=0 EndX=-17.7513 EndY=28 EndZ=0
    g3: LineSegment StartX=-17.7513 StartY=28 StartZ=0 EndX=-11.8564 EndY=50 EndZ=0
    g4: LineSegment StartX=-11.8564 StartY=50 StartZ=0 EndX=11.8564 EndY=50 EndZ=0
    g5: LineSegment StartX=11.8564 StartY=50 StartZ=0 EndX=17.7513 EndY=28 EndZ=0
    g6: LineSegment StartX=17.7513 StartY=28 StartZ=0 EndX=34 EndY=17.5 EndZ=0
    g7: LineSegment StartX=-23 StartY=-29 StartZ=0 EndX=23 EndY=-29 EndZ=0
    g8: LineSegment [constr] StartX=-34 StartY=17.5 StartZ=0 EndX=34 EndY=17.5 EndZ=0
    g9: LineSegment [constr] StartX=-17.7513 StartY=28 StartZ=0 EndX=17.7513 EndY=28 EndZ=0
    g10: LineSegment StartX=-34 StartY=17.5 StartZ=0 EndX=-34 EndY=16.5 EndZ=0
    g11: LineSegment [constr] StartX=-34 StartY=16.5 StartZ=0 EndX=-20 EndY=16.5 EndZ=0
    g12: LineSegment [constr] StartX=-20 StartY=16.5 StartZ=0 EndX=-20 EndY=-14.5 EndZ=0
    g13: LineSegment [constr] StartX=-20 StartY=-14.5 StartZ=0 EndX=-34 EndY=-14.5 EndZ=0
    g14: LineSegment StartX=-34 StartY=-14.5 StartZ=0 EndX=-34 EndY=-15.5 EndZ=0
    g15: LineSegment StartX=34 StartY=17.5 StartZ=0 EndX=34 EndY=16.5 EndZ=0
    g16: LineSegment [constr] StartX=34 StartY=16.5 StartZ=0 EndX=20 EndY=16.5 EndZ=0
    g17: LineSegment [constr] StartX=20 StartY=16.5 StartZ=0 EndX=20 EndY=-14.5 EndZ=0
    g18: LineSegment [constr] StartX=20 StartY=-14.5 StartZ=0 EndX=34 EndY=-14.5 EndZ=0
    g19: LineSegment StartX=34 StartY=-14.5 StartZ=0 EndX=34 EndY=-15.5 EndZ=0
    g20: LineSegment StartX=-34 StartY=16.5 StartZ=0 EndX=-34 EndY=-14.5 EndZ=0
    g21: LineSegment StartX=34 StartY=16.5 StartZ=0 EndX=34 EndY=-14.5 EndZ=0
  constraints (62):
    c: Coincident(g2,g3)
    c: Coincident(g3,g4)
    c: Horizontal(g4)
    c: Coincident(g4,g5)
    c: Coincident(g5,g6)
    c: Equal(g1,g0)
    c: DistanceX(g0,g1) = 68
    c: Equal(g2,g6)
    c: Horizontal(g8)
    c: Equal(g3,g5)
    c: DistanceX(g2,g-1) = 34
    c: DistanceY(g-1,g2) = 17.5
    c: DistanceY(g-1,g5) = 28
    c: Angle(g3,g4) = 1.8326
    c: Coincident(g9,g2)
    c: Coincident(g9,g5)
    c: Horizontal(g9)
    c: Coincident(g1,g7)
    c: Coincident(g0,g7)
    c: Horizontal(g7)
    c: DistanceY(g-1,g3) = 50
    c: Distance(g7) = 46
    c: DistanceY(g1,g4) = 79
    c: DistanceY(g0,g2) = 33
    c: Coincident(g2,g10)
    c: Vertical(g10)
    c: Coincident(g10,g11)
    c: Horizontal(g11)
    c: Coincident(g11,g12)
    c: Vertical(g12)
    c: Coincident(g12,g13)
    c: Horizontal(g13)
    c: Coincident(g13,g14)
    c: Coincident(g14,g0)
    c: Vertical(g14)
    c: Equal(g10,g14)
    c: Distance(g12) = 31
    c: Distance(g11) = 14
    c: Coincident(g6,g15)
    c: Vertical(g15)
    c: Coincident(g15,g16)
    c: Horizontal(g16)
    c: Coincident(g16,g17)
    c: Vertical(g17)
    c: Coincident(g17,g18)
    c: Coincident(g18,g19)
    c: Vertical(g19)
    c: Coincident(g1,g19)
    c: Horizontal(g18)
    c: Equal(g14,g15)
    c: Equal(g15,g19)
    c: Equal(g17,g12)
    c: Equal(g13,g18)
    c: Equal(g16,g11)
    c: Equal(g16,g18)
    c: Coincident(g8,g6)
    c: Coincident(g8,g2)
    c: Coincident(g20,g10)
    c: Coincident(g20,g13)
    c: Coincident(g21,g15)
    c: Coincident(g21,g18)
    c: Distance(g9) = 35.5026
FEATURE [PartDesign::Pad] Pad019
  Length = 50
  Length2 = 100
  Placement = pos=(0,0,40) rot=(0,0,1;0rad)
  Reversed = true
  Sketch = -> Sketch031
  Type = 0
FEATURE [Sketcher::SketchObject] Sketch032
  Placement = pos=(36,0,1) rot=(0.57735,0.57735,0.57735;2.0944rad)
  sketch-geometry (9):
    g0: LineSegment StartX=-29 StartY=34 StartZ=0 EndX=-29 EndY=-8 EndZ=0
    g1: LineSegment StartX=-29 StartY=-8 StartZ=0 EndX=41 EndY=-8 EndZ=0
    g2: LineSegment StartX=41 StartY=-8 StartZ=0 EndX=43 EndY=0 EndZ=0
    g3: LineSegment StartX=43 StartY=0 StartZ=0 EndX=43 EndY=20.7789 EndZ=0
    g4: LineSegment StartX=41.339 StartY=22.75 StartZ=0 EndX=4.15272 EndY=29.1455 EndZ=0
    g5: LineSegment StartX=-23.0408 StartY=29.7837 StartZ=0 EndX=-29 EndY=34 EndZ=0
    g6: ArcOfCircle CenterX=-14.0883 CenterY=42.4369 CenterZ=0 NormalX=0 NormalY=0 NormalZ=1 Radius=15.5 StartAngle=4.09663 EndAngle=5.07232
    g7: ArcOfCircle CenterX=0 CenterY=5 CenterZ=0 NormalX=0 NormalY=0 NormalZ=1 Radius=24.5 StartAngle=1.40048 EndAngle=1.93072
    g8: ArcOfCircle CenterX=41 CenterY=20.7789 CenterZ=0 NormalX=0 NormalY=0 NormalZ=1 Radius=2 StartAngle=0 EndAngle=1.40048
  constraints (28):
    c: Vertical(g0)
    c: Coincident(g0,g1)
    c: Horizontal(g1)
    c: Coincident(g1,g2)
    c: Tangent(g5,g6)
    c: Coincident(g6,g7)
    c: Tangent(g6,g7)
    c: DistanceY(g0,g5) = 42
    c: DistanceY(g0,g-1) = 8
    c: Coincident(g7,g4)
    c: Tangent(g7,g4)
    c: PointOnObject(g7,g-2)
    c: Distance(g-1,g7) = 5
    c: Coincident(g5,g6)
    c: Tangent(g4,g8) = -1.5708
    c: Tangent(g3,g8) = -1.5708
    c: Vertical(g3)
    c: Coincident(g0,g5)
    c: DistanceX(g0,g-1) = 29
    c: DistanceX(g-1,g3) = 43
    c: Distance(g1) = 70
    c: Coincident(g2,g3)
    c: DistanceY(g2,g-1) = 0
    c: Radius(g8) = 2
    c: Radius(g7) = 24.5
    c: Radius(g6) = 15.5
    c: Distance(g5) = 7.3
    c: DistanceY(g-1,g4) = 22.75
FEATURE [PartDesign::Pad] Pad020
  Length = 75
  Length2 = 100
  Placement = pos=(36,0,1) rot=(0.57735,0.57735,0.57735;2.0944rad)
  Reversed = true
  Sketch = -> Sketch032
  Type = 0
FEATURE [Part::MultiCommon] Common001
  Shapes = -> [Pad020,Pad019]
FEATURE [Part::Cut] Cut021
  Base = -> Cut020
  Tool = -> Common001
FEATURE [Part::Chamfer] Chamfer059
  Base = -> Cut021
  Edges = 2 edges r=3: [Edge52,Edge69]
FEATURE [Part::Mirroring] Part__Mirroring003  label="Cut018 (Mirror #4)"
  Base = (0,0,0)
  Normal = (1,0,0)
  Source = -> Cut018
FEATURE [Sketcher::SketchObject] Sketch033
  Placement = pos=(0,0,25.25) rot=(0,0,1;0rad)
  sketch-geometry (5):
    g0: LineSegment StartX=-22.5 StartY=-15.5 StartZ=0 EndX=-22.5 EndY=-27.5 EndZ=0
    g1: LineSegment StartX=-22.5 StartY=-27.5 StartZ=0 EndX=-22.8061 EndY=-27.5 EndZ=0
    g2: LineSegment StartX=-35 StartY=-16.9 StartZ=0 EndX=-35 EndY=-15.5 EndZ=0
    g3: LineSegment StartX=-35 StartY=-15.5 StartZ=0 EndX=-22.5 EndY=-15.5 EndZ=0
    g4: LineSegment StartX=-35 StartY=-16.9 StartZ=0 EndX=-22.8061 EndY=-27.5 EndZ=0
  constraints (15):
    c: Coincident(g0,g1)
    c: Horizontal(g1)
    c: Vertical(g0)
    c: DistanceY(g0,g-1) = 15.5
    c: Distance(g0) = 12
    c: Vertical(g2)
    c: Coincident(g3,g2)
    c: Coincident(g3,g0)
    c: Horizontal(g3)
    c: Coincident(g4,g2)
    c: Coincident(g4,g1)
    c: Distance(g2) = 1.4
    c: Angle(g4,g2) = 2.28638
    c: DistanceX(g0,g-1) = 22.5
    c: Distance(g3) = 12.5
FEATURE [PartDesign::Pad] Pad021
  Length = 31
  Length2 = 100
  Placement = pos=(0,0,25.25) rot=(0,0,1;0rad)
  Sketch = -> Sketch033
  Type = 0
FEATURE [Part::Cylinder] Cylinder033
  Angle = 360
  Height = 24
  Placement = pos=(-26,-18,16) rot=(0,0,1;0rad)
  Radius = 1.75
FEATURE [Part::Cylinder] Cylinder034
  Angle = 360
  Height = 24
  Placement = pos=(-26,-18,26.75) rot=(0,0,1;0rad)
  Radius = 3.5
FEATURE [Part::MultiFuse] Fusion021
  Shapes = -> [Cylinder033,Cylinder034]
FEATURE [Part::FeaturePython] Clone037  label="Clone of Cut020"  # Draft clone (typed FeaturePython)
  Objects = -> [Cut020]
  Scale = (1,1,1)
FEATURE [Part::Cylinder] Cylinder035
  Angle = 360
  Height = 24
  Placement = pos=(-26,-18,25.25) rot=(0,0,1;0rad)
  Radius = 5
FEATURE [Part::MultiFuse] Fusion022
  Shapes = -> [Pad021,Cylinder035]
FEATURE [Part::MultiCommon] Common002
  Shapes = -> [Fusion022,Clone037]
FEATURE [Part::Mirroring] Part__Mirroring004  label="Common002 (Mirror #5)"
  Base = (0,0,0)
  Normal = (1,0,0)
  Source = -> Common002
FEATURE [Part::MultiFuse] Fusion023
  Shapes = -> [Common002,Part__Mirroring004]
FEATURE [Part::MultiFuse] Fusion024
  Shapes = -> [Fusion023,Chamfer059]
FEATURE [Part::Mirroring] Part__Mirroring005  label="Fusion021 (Mirror #6)"
  Base = (0,0,0)
  Normal = (1,0,0)
  Source = -> Fusion021
FEATURE [Part::MultiFuse] Fusion025
  Shapes = -> [Fusion021,Part__Mirroring005]
FEATURE [Part::Cut] Cut022
  Base = -> Fusion024
  Tool = -> Fusion025
FEATURE [Sketcher::SketchObject] Sketch035
  Placement = pos=(0,0,20) rot=(0,0,1;0rad)
  sketch-geometry (4):
    g0: ArcOfCircle CenterX=-16.5 CenterY=-3 CenterZ=0 NormalX=0 NormalY=0 NormalZ=1 Radius=5 StartAngle=6.28319 EndAngle=9.42478
    g1: ArcOfCircle CenterX=-16.5 CenterY=-13 CenterZ=0 NormalX=0 NormalY=0 NormalZ=1 Radius=5 StartAngle=3.14159 EndAngle=6.28319
    g2: LineSegment StartX=-21.5 StartY=-3 StartZ=0 EndX=-21.5 EndY=-13 EndZ=0
    g3: LineSegment StartX=-11.5 StartY=-3 StartZ=0 EndX=-11.5 EndY=-13 EndZ=0
  constraints (14):
    c: Coincident(g2,g0)
    c: Coincident(g2,g1)
    c: Vertical(g2)
    c: Coincident(g3,g1)
    c: Coincident(g0,g3)
    c: Vertical(g3)
    c: Equal(g0,g1)
    c: Tangent(g0,g2)
    c: Equal(g2,g3)
    c: Tangent(g0,g3)
    c: Radius(g0) = 5
    c: Distance(g3) = 10
    c: DistanceX(g0,g-1) = 16.5
    c: DistanceY(g1,g-1) = 13
FEATURE [PartDesign::Pad] Pad022
  Length = 15
  Length2 = 100
  Placement = pos=(0,0,20) rot=(0,0,1;0rad)
  Sketch = -> Sketch035
  Type = 0
FEATURE [Sketcher::SketchObject] Sketch036
  Placement = pos=(0,0,26) rot=(0,0,1;0rad)
  sketch-geometry (4):
    g0: ArcOfCircle CenterX=-16.5 CenterY=-3 CenterZ=0 NormalX=0 NormalY=0 NormalZ=1 Radius=6 StartAngle=6.265e-09 EndAngle=3.14159
    g1: ArcOfCircle CenterX=-16.5 CenterY=-13 CenterZ=0 NormalX=0 NormalY=0 NormalZ=1 Radius=6 StartAngle=3.14159 EndAngle=6.28318
    g2: LineSegment StartX=-22.5 StartY=-3 StartZ=0 EndX=-22.5 EndY=-13 EndZ=0
    g3: LineSegment StartX=-10.5 StartY=-3 StartZ=0 EndX=-10.5 EndY=-13 EndZ=0
  constraints (14):
    c: Coincident(g2,g0)
    c: Coincident(g2,g1)
    c: Vertical(g2)
    c: Coincident(g3,g1)
    c: Coincident(g0,g3)
    c: Vertical(g3)
    c: Equal(g0,g1)
    c: Tangent(g0,g2)
    c: Equal(g2,g3)
    c: Tangent(g0,g3)
    c: Radius(g0) = 6
    c: Distance(g3) = 10
    c: DistanceX(g0,g-1) = 16.5
    c: DistanceY(g1,g-1) = 13
FEATURE [Part::Mirroring] Part__Mirroring006  label="Pad022 (Mirror #7)"
  Base = (0,0,0)
  Normal = (1,0,0)
  Source = -> Pad022
FEATURE [Part::MultiFuse] Fusion026
  Shapes = -> [Pad022,Part__Mirroring006]
FEATURE [Part::Cut] Cut023
  Base = -> Cut022
  Tool = -> Fusion026
FEATURE [Sketcher::SketchObject] Sketch037
  Placement = pos=(0,0,28) rot=(0,0,1;0rad)
  sketch-geometry (5):
    g0: ArcOfCircle CenterX=-16.5 CenterY=-2.99999 CenterZ=0 NormalX=0 NormalY=0 NormalZ=1 Radius=4 StartAngle=6.28318 EndAngle=9.42478
    g1: ArcOfCircle CenterX=-16.5 CenterY=-13 CenterZ=0 NormalX=0 NormalY=0 NormalZ=1 Radius=4 StartAngle=3.1416 EndAngle=6.28318
    g2: LineSegment StartX=-20.5 StartY=-3.00001 StartZ=0 EndX=-20.5 EndY=-13 EndZ=0
    g3: LineSegment StartX=-12.5 StartY=-3.00001 StartZ=0 EndX=-12.5 EndY=-13 EndZ=0
    g4: LineSegment [constr] StartX=-20.5 StartY=-13 StartZ=0 EndX=-12.5 EndY=-13 EndZ=0
  constraints (16):
    c: Coincident(g2,g0)
    c: Coincident(g2,g1)
    c: Vertical(g2)
    c: Coincident(g3,g1)
    c: Coincident(g0,g3)
    c: Vertical(g3)
    c: Equal(g0,g1)
    c: Equal(g2,g3)
    c: Tangent(g0,g3)
    c: Radius(g0) = 4
    c: Distance(g3) = 10
    c: DistanceX(g0,g-1) = 16.5
    c: DistanceY(g1,g-1) = 13
    c: Coincident(g4,g1)
    c: Coincident(g4,g1)
    c: Horizontal(g4)
FEATURE [PartDesign::Pad] Pad023
  Length = 15
  Length2 = 100
  Placement = pos=(0,0,26) rot=(0,0,1;0rad)
  Sketch = -> Sketch036
  Type = 0
FEATURE [Part::FeaturePython] Clone040  label="Clone of Common"  # Draft clone (typed FeaturePython)
  Objects = -> [Common]
  Scale = (1,1,1)
FEATURE [Part::MultiCommon] Common003
  Shapes = -> [Pad023,Clone040]
FEATURE [PartDesign::Pad] Pad024
  Length = 20
  Length2 = 100
  Placement = pos=(0,0,28) rot=(0,0,1;0rad)
  Sketch = -> Sketch037
  Type = 0
FEATURE [Part::Cut] Cut024
  Base = -> Common003
  Tool = -> Pad024
FEATURE [Part::Mirroring] Part__Mirroring007  label="Cut024 (Mirror #8)"
  Base = (0,0,0)
  Normal = (1,0,0)
  Source = -> Cut024
FEATURE [Part::MultiFuse] Fusion027
  Shapes = -> [Cut024,Part__Mirroring007]
FEATURE [Part::MultiFuse] Fusion028
  Shapes = -> [Cut023,Fusion027]
FEATURE [Part::Chamfer] Chamfer060
  Base = -> Fusion028
  Edges = 2 edges r=1: [Edge16,Edge51]
FEATURE [Part::Fillet] Fillet011
  Base = -> Chamfer060
  Edges = 4 edges r=0.6: [Edge204,Edge206,Edge226,Edge228]
FEATURE [Part::Fillet] Fillet012
  Base = -> Fillet011
  Edges = 1 edges r=1: [Edge124]
FEATURE [Part::Chamfer] Chamfer061
  Base = -> Fillet012
  Edges = 2 edges r=4: [Edge42,Edge71]
FEATURE [Sketcher::SketchObject] Sketch038
  Placement = pos=(24.5622,6.55,0) rot=(0.476905,0.621515,0.621515;2.2516rad)
  sketch-geometry (4):
    g0: LineSegment StartX=27.5 StartY=19 StartZ=0 EndX=36.5 EndY=19 EndZ=0
    g1: LineSegment StartX=36.5 StartY=19 StartZ=0 EndX=36.5 EndY=-1 EndZ=0
    g2: LineSegment StartX=36.5 StartY=-1 StartZ=0 EndX=27.5 EndY=-1 EndZ=0
    g3: LineSegment StartX=27.5 StartY=-1 StartZ=0 EndX=27.5 EndY=19 EndZ=0
  constraints (12):
    c: Coincident(g0,g1)
    c: Coincident(g1,g2)
    c: Coincident(g2,g3)
    c: Coincident(g3,g0)
    c: Horizontal(g0)
    c: Horizontal(g2)
    c: Vertical(g1)
    c: Vertical(g3)
    c: Distance(g1) = 20
    c: Distance(g0) = 9
    c: DistanceX(g-1,g2) = 27.5
    c: DistanceY(g2,g-1) = 1
FEATURE [Sketcher::SketchObject] Sketch039
  Placement = pos=(22.5622,6.1,0) rot=(0.476905,0.621515,0.621515;2.2516rad)
  sketch-geometry (4):
    g0: LineSegment StartX=28.5 StartY=20.5 StartZ=0 EndX=38 EndY=20.5 EndZ=0
    g1: LineSegment StartX=38 StartY=20.5 StartZ=0 EndX=38 EndY=-2.5 EndZ=0
    g2: LineSegment StartX=38 StartY=-2.5 StartZ=0 EndX=28.5 EndY=-2.5 EndZ=0
    g3: LineSegment StartX=28.5 StartY=-2.5 StartZ=0 EndX=28.5 EndY=20.5 EndZ=0
  constraints (12):
    c: Coincident(g0,g1)
    c: Coincident(g1,g2)
    c: Coincident(g2,g3)
    c: Coincident(g3,g0)
    c: Horizontal(g0)
    c: Horizontal(g2)
    c: Vertical(g1)
    c: Vertical(g3)
    c: DistanceX(g-1,g0) = 28.5
    c: Distance(g0) = 9.5
    c: Distance(g1) = 23
    c: DistanceY(g2,g-1) = 2.5
FEATURE [PartDesign::Pad] Pad025
  Length = 10
  Length2 = 100
  Placement = pos=(24.5622,6.55,0) rot=(0.476905,0.621515,0.621515;2.2516rad)
  Reversed = true
  Sketch = -> Sketch038
  Type = 0
FEATURE [PartDesign::Pad] Pad026
  Length = 3
  Length2 = 100
  Placement = pos=(22.5622,6.1,0) rot=(0.476905,0.621515,0.621515;2.2516rad)
  Reversed = true
  Sketch = -> Sketch039
  Type = 0
FEATURE [Part::Mirroring] Part__Mirroring008  label="Pad026 (Mirror #9)"
  Base = (0,0,0)
  Normal = (1,0,0)
  Source = -> Pad026
FEATURE [Part::MultiFuse] Fusion029
  Shapes = -> [Pad026,Part__Mirroring008]
FEATURE [Part::MultiFuse] Fusion030
  Shapes = -> [Fusion029,Chamfer061]
FEATURE [Part::Mirroring] Part__Mirroring009  label="Pad025 (Mirror #10)"
  Base = (0,0,0)
  Normal = (1,0,0)
  Source = -> Pad025
FEATURE [Part::MultiFuse] Fusion031
  Shapes = -> [Pad025,Part__Mirroring009]
FEATURE [Sketcher::SketchObject] Sketch040
  Placement = pos=(0,0,-10) rot=(1,0,0;3.14159rad)
  sketch-geometry (6):
    g0: LineSegment StartX=-35.7762 StartY=-13.4731 StartZ=0 EndX=-35.7762 EndY=-18.7028 EndZ=0
    g1: LineSegment StartX=-35.7762 StartY=-18.7028 StartZ=0 EndX=-19.3803 EndY=-28.0643 EndZ=0
    g2: LineSegment StartX=-19.3803 StartY=-28.0643 StartZ=0 EndX=19.3803 EndY=-28.0643 EndZ=0
    g3: LineSegment StartX=19.3803 StartY=-28.0643 StartZ=0 EndX=35.7762 EndY=-18.7028 EndZ=0
    g4: LineSegment StartX=35.7762 StartY=-18.7028 StartZ=0 EndX=35.7762 EndY=-13.4731 EndZ=0
    g5: LineSegment StartX=35.7762 StartY=-13.4731 StartZ=0 EndX=-35.7762 EndY=-13.4731 EndZ=0
  constraints (12):
    c: Vertical(g0)
    c: Coincident(g0,g1)
    c: Coincident(g1,g2)
    c: Horizontal(g2)
    c: Coincident(g2,g3)
    c: Coincident(g3,g4)
    c: Vertical(g4)
    c: Coincident(g4,g5)
    c: Coincident(g5,g0)
    c: Equal(g0,g4)
    c: Equal(g3,g1)
    c: Symmetric(g4,g0,g-2)
FEATURE [PartDesign::Pad] Pad027
  Length = 5.5
  Length2 = 100
  Placement = pos=(0,0,-10) rot=(1,0,0;3.14159rad)
  Reversed = true
  Sketch = -> Sketch040
  Type = 0
FEATURE [Part::MultiFuse] Fusion032
  Shapes = -> [Fusion030,Cut018,Part__Mirroring003]
FEATURE [Part::Cut] Cut025
  Base = -> Fusion032
  Tool = -> Pad027
FEATURE [Part::Cut] Cut026
  Base = -> Cut025
  Tool = -> Fusion031
FEATURE [Part::Cylinder] Cylinder036
  Angle = 360
  Height = 16
  Radius = 10.5
FEATURE [Part::Cylinder] Cylinder037
  Angle = 360
  Height = 16
  Placement = pos=(0,0,4) rot=(0,0,1;0rad)
  Radius = 10
FEATURE [Part::Cylinder] Cylinder038
  Angle = 360
  Height = 30
  Placement = pos=(0,0,-10) rot=(0,0,1;0rad)
  Radius = 1.55
FEATURE [Part::Cylinder] Cylinder039
  Angle = 360
  Height = 30
  Placement = pos=(7,0,-10) rot=(0,0,1;0rad)
  Radius = 2.25
FEATURE [Part::FeaturePython] Array002  # Draft array (typed FeaturePython)
  Angle = 360
  ArrayType = 1
  Axis = (0,0,1)
  Base = -> Cylinder039
  Center = (0,0,0)
  Fuse = false
  IntervalAxis = (0,0,0)
  IntervalX = (1,0,0)
  IntervalY = (0,1,0)
  IntervalZ = (0,0,0)
  NumberPolar = 8
  NumberX = 2
  NumberY = 2
  NumberZ = 1
FEATURE [Part::MultiFuse] Fusion033
  Shapes = -> [Cylinder038,Array002]
FEATURE [Part::Cylinder] Cylinder040
  Angle = 360
  Height = 16
  Radius = 13.75
FEATURE [Part::Cylinder] Cylinder041
  Angle = 360
  Height = 20
  Placement = pos=(0,0,-1) rot=(0,0,1;0rad)
  Radius = 10.5
FEATURE [Part::Cut] Cut027
  Base = -> Cylinder040
  Tool = -> Cylinder041
FEATURE [Part::Fillet] Fillet013  label="tire-src001"
  Base = -> Cut027
  Edges = 2 edges r=0.7: [Edge1,Edge3]
FEATURE [Part::Cylinder] Cylinder042
  Angle = 360
  Height = 16
  Placement = pos=(0,0,-13) rot=(0,0,1;0rad)
  Radius = 10
FEATURE [Part::Cylinder] Cylinder043
  Angle = 360
  Height = 5.5
  Placement = pos=(0,0,-2) rot=(0,0,1;0rad)
  Radius = 3.5
FEATURE [Part::Cylinder] Cylinder044
  Angle = 360
  Height = 5.5
  Placement = pos=(0,0,3.5) rot=(0,0,1;0rad)
  Radius = 2
FEATURE [Part::Cylinder] Cylinder045
  Angle = 360
  Height = 32
  Placement = pos=(0,15,0.25) rot=(1,0,0;1.5708rad)
  Radius = 1.25
FEATURE [Part::MultiFuse] Fusion034
  Shapes = -> [Cylinder037,Cylinder042]
FEATURE [Part::Cut] Cut028
  Base = -> Cylinder036
  Tool = -> Fusion034
FEATURE [Part::MultiFuse] Fusion035
  Shapes = -> [Cylinder044,Cylinder043,Cut028]
FEATURE [Part::Cut] Cut002
  Base = -> Fusion035
  Tool = -> Cylinder045
FEATURE [Part::Cut] Cut029
  Base = -> Cut002
  Tool = -> Fusion033
FEATURE [Part::Chamfer] Chamfer062
  Base = -> Cut029
  Edges = 3 edges: [Edge2 r=0.1,Edge6 r=0.3,Edge20 r=0.2]
FEATURE [Image::ImagePlane] ImagePlane
  Placement = pos=(0,0,16) rot=(0,0,1;0rad)
  XSize = 24.321
  YSize = 25.058
FEATURE [Part::FeaturePython] Clone043  label="Clone of tire-src002"  # Draft clone (typed FeaturePython)
  Objects = -> [Fillet013]
  Placement = pos=(34,0,5) rot=(0,1,0;1.5708rad)
  Scale = (1,1,1)
FEATURE [Part::FeaturePython] Clone044  label="Clone of Chamfer062"  # Draft clone (typed FeaturePython)
  Objects = -> [Chamfer062]
  Placement = pos=(34,0,5) rot=(0,1,0;1.5708rad)
  Scale = (1,1,1)
FEATURE [Part::FeaturePython] Clone045  label="Clone of tire-src003"  # Draft clone (typed FeaturePython)
  Objects = -> [Fillet013]
  Placement = pos=(-34,0,5) rot=(0,-1,0;1.5708rad)
  Scale = (1,1,1)
FEATURE [Part::FeaturePython] Clone046  label="Clone of Chamfer063"  # Draft clone (typed FeaturePython)
  Objects = -> [Chamfer062]
  Placement = pos=(-34,0,5) rot=(0,-1,0;1.5708rad)
  Scale = (1,1,1)
FEATURE [Image::ImagePlane] ImagePlane001
  Placement = pos=(50,0,5) rot=(0,1,0;1.5708rad)
  XSize = 24.321
  YSize = 25.058
FEATURE [Image::ImagePlane] ImagePlane002
  Placement = pos=(-50,0,5) rot=(0,-1,0;1.5708rad)
  XSize = 24.321
  YSize = 25.058
FEATURE [Part::MultiFuse] Fusion036
  Shapes = -> [Pad011,Box011]
FEATURE [Part::Cylinder] Cylinder046
  Angle = 360
  Height = 12
  Placement = pos=(16.5,-13,16) rot=(0,0,1;0rad)
  Radius = 2
FEATURE [Part::Cylinder] Cylinder047
  Angle = 360
  Height = 14
  Placement = pos=(16.5,-3,16) rot=(0,0,1;0rad)
  Radius = 2
FEATURE [Sketcher::SketchObject] Sketch041  label="main-body-sketch"
  sketch-geometry (8):
    g0: LineSegment StartX=-2.9 StartY=3.1 StartZ=0 EndX=2.9 EndY=3.1 EndZ=0
    g1: LineSegment StartX=3.1 StartY=2.9 StartZ=0 EndX=3.1 EndY=-2.9 EndZ=0
    g2: LineSegment StartX=2.9 StartY=-3.1 StartZ=0 EndX=-2.9 EndY=-3.1 EndZ=0
    g3: LineSegment StartX=-3.1 StartY=-2.9 StartZ=0 EndX=-3.1 EndY=2.9 EndZ=0
    g4: ArcOfCircle CenterX=-2.9 CenterY=2.9 CenterZ=0 NormalX=0 NormalY=0 NormalZ=1 Radius=0.2 StartAngle=1.5708 EndAngle=3.14159
    g5: ArcOfCircle CenterX=2.9 CenterY=2.9 CenterZ=0 NormalX=0 NormalY=0 NormalZ=1 Radius=0.2 StartAngle=0 EndAngle=1.5708
    g6: ArcOfCircle CenterX=2.9 CenterY=-2.9 CenterZ=0 NormalX=0 NormalY=0 NormalZ=1 Radius=0.2 StartAngle=4.71239 EndAngle=6.28319
    g7: ArcOfCircle CenterX=-2.9 CenterY=-2.9 CenterZ=0 NormalX=0 NormalY=0 NormalZ=1 Radius=0.2 StartAngle=3.14159 EndAngle=4.71239
  constraints (19):
    c: Horizontal(g0)
    c: Horizontal(g2)
    c: Vertical(g1)
    c: Vertical(g3)
    c: Equal(g0,g1)
    c: Tangent(g0,g4)
    c: Tangent(g3,g4)
    c: Radius(g4) = 0.2
    c: Tangent(g0,g5)
    c: Tangent(g1,g5)
    c: Tangent(g1,g6)
    c: Tangent(g2,g6)
    c: Tangent(g2,g7)
    c: Tangent(g3,g7)
    c: Symmetric(g4,g6,g-1)
    c: Equal(g5,g4)
    c: Equal(g4,g7)
    c: Equal(g7,g6)
    c: DistanceX(g3,g1) = 6.2
FEATURE [PartDesign::Pad] Pad028  label="main-body"
  Length = 3.2
  Length2 = 100
  Sketch = -> Sketch041
  Type = 0
FEATURE [Sketcher::SketchObject] Sketch001  label="bottom-legs-sketch"
  ExternalGeometry = -> [Pad028]
  Placement = pos=(0,0,0) rot=(1,0,0;3.14159rad)
  Support = -> Pad028 [Face9]
  sketch-geometry (16):
    g0: LineSegment StartX=-2.8 StartY=3 StartZ=0 EndX=-1.5 EndY=3 EndZ=0
    g1: LineSegment StartX=-1.5 StartY=3 StartZ=0 EndX=-1.5 EndY=1 EndZ=0
    g2: LineSegment StartX=-1.5 StartY=1 StartZ=0 EndX=-2.8 EndY=1 EndZ=0
    g3: LineSegment StartX=-2.8 StartY=1 StartZ=0 EndX=-2.8 EndY=3 EndZ=0
    g4: LineSegment StartX=1.5 StartY=3 StartZ=0 EndX=2.8 EndY=3 EndZ=0
    g5: LineSegment StartX=2.8 StartY=3 StartZ=0 EndX=2.8 EndY=1 EndZ=0
    g6: LineSegment StartX=2.8 StartY=1 StartZ=0 EndX=1.5 EndY=1 EndZ=0
    g7: LineSegment StartX=1.5 StartY=1 StartZ=0 EndX=1.5 EndY=3 EndZ=0
    g8: LineSegment StartX=-2.8 StartY=-1 StartZ=0 EndX=-1.5 EndY=-1 EndZ=0
    g9: LineSegment StartX=-1.5 StartY=-1 StartZ=0 EndX=-1.5 EndY=-3 EndZ=0
    g10: LineSegment StartX=-1.5 StartY=-3 StartZ=0 EndX=-2.8 EndY=-3 EndZ=0
    g11: LineSegment StartX=-2.8 StartY=-3 StartZ=0 EndX=-2.8 EndY=-1 EndZ=0
    g12: LineSegment StartX=1.5 StartY=-1 StartZ=0 EndX=2.8 EndY=-1 EndZ=0
    g13: LineSegment StartX=2.8 StartY=-1 StartZ=0 EndX=2.8 EndY=-3 EndZ=0
    g14: LineSegment StartX=2.8 StartY=-3 StartZ=0 EndX=1.5 EndY=-3 EndZ=0
    g15: LineSegment StartX=1.5 StartY=-3 StartZ=0 EndX=1.5 EndY=-1 EndZ=0
  constraints (45):
    c: Coincident(g0,g1)
    c: Coincident(g1,g2)
    c: Coincident(g2,g3)
    c: Coincident(g3,g0)
    c: Horizontal(g0)
    c: Horizontal(g2)
    c: Vertical(g1)
    c: Vertical(g3)
    c: DistanceX(g0) = 1.3
    c: DistanceY(g1) = -2
    c: DistanceX(g-3,g2) = 0.3
    c: DistanceY(g0,g-4) = 0.1
    c: Coincident(g4,g5)
    c: Coincident(g5,g6)
    c: Coincident(g6,g7)
    c: Coincident(g7,g4)
    c: Horizontal(g4)
    c: Horizontal(g6)
    c: Vertical(g5)
    c: Vertical(g7)
    c: Coincident(g8,g9)
    c: Coincident(g9,g10)
    c: Coincident(g10,g11)
    c: Coincident(g11,g8)
    c: Horizontal(g8)
    c: Horizontal(g10)
    c: Vertical(g9)
    c: Vertical(g11)
    c: Coincident(g12,g13)
    c: Coincident(g13,g14)
    c: Coincident(g14,g15)
    c: Coincident(g15,g12)
    c: Horizontal(g12)
    c: Horizontal(g14)
    c: Vertical(g13)
    c: Vertical(g15)
    c: Equal(g0,g4)
    c: Equal(g4,g12)
    c: Equal(g12,g8)
    c: Equal(g1,g7)
    c: Equal(g7,g9)
    c: Equal(g9,g15)
    c: Symmetric(g0,g10,g-1)
    c: Symmetric(g13,g10,g-2)
    c: Symmetric(g4,g13,g-1)
FEATURE [PartDesign::Pad] Pad029  label="botom-legs"
  Length = 0.2
  Length2 = 100
  Sketch = -> Sketch001
  Type = 0
FEATURE [Sketcher::SketchObject] Sketch042  label="button-sketch"
  Placement = pos=(0,0,3.2) rot=(0,0,1;0rad)
  Support = -> Pad029 [Face5]
  sketch-geometry (1):
    g0: Circle CenterX=0 CenterY=0 CenterZ=0 NormalX=0 NormalY=0 NormalZ=1 Radius=1.7
  constraints (2):
    c: Radius(g0) = 1.7
    c: Coincident(g0,g-1)
FEATURE [PartDesign::Pad] Pad030  label="button"
  Length = 8.8
  Length2 = 100
  Sketch = -> Sketch042
  Type = 0
FEATURE [Sketcher::SketchObject] Sketch043  label="top-pins-sketch"
  ExternalGeometry = -> [Pad030]
  Placement = pos=(0,0,3.2) rot=(0,0,1;0rad)
  Support = -> Pad030 [Face5]
  sketch-geometry (4):
    g0: Circle CenterX=-2.3 CenterY=2.3 CenterZ=0 NormalX=0 NormalY=0 NormalZ=1 Radius=0.6
    g1: Circle CenterX=2.3 CenterY=2.3 CenterZ=0 NormalX=0 NormalY=0 NormalZ=1 Radius=0.6
    g2: Circle CenterX=-2.3 CenterY=-2.3 CenterZ=0 NormalX=0 NormalY=0 NormalZ=1 Radius=0.6
    g3: Circle CenterX=2.3 CenterY=-2.3 CenterZ=0 NormalX=0 NormalY=0 NormalZ=1 Radius=0.6
  constraints (9):
    c: Radius(g0) = 0.6
    c: DistanceX(g0,g-3) = -0.8
    c: DistanceY(g0,g-4) = 0.8
    c: Equal(g0,g1)
    c: Equal(g1,g3)
    c: Equal(g3,g2)
    c: Symmetric(g0,g1,g-2)
    c: Symmetric(g0,g2,g-1)
    c: Symmetric(g2,g3,g-2)
FEATURE [PartDesign::Pad] Pad031  label="top-pins"
  Length = 0.3
  Length2 = 100
  Sketch = -> Sketch043
  Type = 0
FEATURE [Part::Feature] Fillet014  label="pin-1"
  Placement = pos=(-3.2,-2.2,0) rot=(1,0,0;1.5708rad)
  shape: bbox 0.922 x 0.7 x 4.6 mm, 20 faces (baked)
FEATURE [Part::Feature] Fillet002  label="pin-002"
  Placement = pos=(-3.2,2.8,0) rot=(1,0,0;1.5708rad)
  shape: bbox 0.922 x 0.7 x 4.6 mm, 20 faces (baked)
FEATURE [Part::Feature] Fillet003  label="pin-003"
  Placement = pos=(3.2,-2.8,0) rot=(0,0.707107,0.707107;3.14159rad)
  shape: bbox 0.922 x 0.7 x 4.6 mm, 20 faces (baked)
FEATURE [Part::Feature] Fillet004  label="pin-004"
  Placement = pos=(3.2,2.2,0) rot=(0,0.707107,0.707107;3.14159rad)
  shape: bbox 0.922 x 0.7 x 4.6 mm, 20 faces (baked)
FEATURE [Part::Feature] Pad003004  label="top-metal-plate001"
  Placement = pos=(0,0,3.2) rot=(0,0,1;0rad)
  shape: bbox 6.2 x 6.2 x 0.2 mm, 15 faces (baked)
FEATURE [Part::Fillet] Fillet005
  Base = -> Pad031
  Edges = 1 edges r=0.1: [Edge79]
FEATURE [Part::Compound] Compound
  Links = -> [Fillet003,Fillet004,Pad003004,Fillet005,Fillet002,Fillet014]
  Placement = pos=(16.6,-3.3,17) rot=(0,0,1;0rad)
FEATURE [Part::FeaturePython] Clone047  label="pushbuttonB"  # Draft clone (typed FeaturePython)
  Objects = -> [Compound]
  Placement = pos=(16.6,-13.4,17) rot=(0,0,1;0rad)
  Scale = (1,1,1)
FEATURE [App::DocumentObjectGroup] Group  label="wheels"
  Group = -> [Clone043,Clone044,Clone045,Clone046,ImagePlane001,ImagePlane002,Clone006,Clone007,Clone008,Clone009]
FEATURE [Part::FeaturePython] Clone048  label="pushbuttonA"  # Draft clone (typed FeaturePython)
  Objects = -> [Compound]
  Placement = pos=(16.6,-3,17) rot=(0,0,1;0rad)
  Scale = (1,1,1)
FEATURE [App::DocumentObjectGroup] Group001  label="bolts"
  Group = -> [Chamfer055,Chamfer056,Chamfer057,Chamfer058]
FEATURE [App::DocumentObjectGroup] Group002  label="src"
  Group = -> [Fillet013,ImagePlane,Cut016,Chamfer062]
FEATURE [Sketcher::SketchObject] Sketch044
  Placement = pos=(-1.5,0,0) rot=(0.57735,0.57735,0.57735;2.0944rad)
  sketch-geometry (6):
    g0: LineSegment StartX=34 StartY=-6 StartZ=0 EndX=37.1429 EndY=5 EndZ=0
    g1: LineSegment StartX=37.1429 StartY=5 StartZ=0 EndX=44 EndY=5 EndZ=0
    g2: LineSegment StartX=44 StartY=5 StartZ=0 EndX=44 EndY=1 EndZ=0
    g3: LineSegment StartX=44 StartY=1 StartZ=0 EndX=42 EndY=1 EndZ=0
    g4: LineSegment StartX=42 StartY=1 StartZ=0 EndX=40 EndY=-6 EndZ=0
    g5: LineSegment StartX=40 StartY=-6 StartZ=0 EndX=34 EndY=-6 EndZ=0
  constraints (18):
    c: Coincident(g0,g1)
    c: Horizontal(g1)
    c: Coincident(g1,g2)
    c: Coincident(g2,g3)
    c: Horizontal(g3)
    c: Coincident(g3,g4)
    c: Coincident(g4,g5)
    c: Coincident(g5,g0)
    c: Horizontal(g5)
    c: Vertical(g2)
    c: Parallel(g4,g0)
    c: Distance(g5) = 6
    c: DistanceY(g0,g-1) = 6
    c: DistanceX(g-1,g2) = 44
    c: Distance(g2) = 4
    c: Distance(g3) = 2
    c: DistanceY(g4,g1) = 11
    c: DistanceX(g4,g2) = 4
FEATURE [PartDesign::Pad] Pad003005
  Length = 3
  Length2 = 100
  Placement = pos=(-1.5,0,0) rot=(0.57735,0.57735,0.57735;2.0944rad)
  Sketch = -> Sketch044
  Type = 0
FEATURE [Sketcher::SketchObject] Sketch045
  Placement = pos=(0,44.2,0) rot=(0,0.707107,0.707107;3.14159rad)
  sketch-geometry (4):
    g0: LineSegment StartX=-2 StartY=6 StartZ=0 EndX=2 EndY=6 EndZ=0
    g1: LineSegment StartX=2 StartY=6 StartZ=0 EndX=2 EndY=0.5 EndZ=0
    g2: LineSegment StartX=2 StartY=0.5 StartZ=0 EndX=-2 EndY=0.5 EndZ=0
    g3: LineSegment StartX=-2 StartY=0.5 StartZ=0 EndX=-2 EndY=6 EndZ=0
  constraints (12):
    c: Coincident(g0,g1)
    c: Coincident(g1,g2)
    c: Coincident(g2,g3)
    c: Coincident(g3,g0)
    c: Horizontal(g0)
    c: Horizontal(g2)
    c: Vertical(g1)
    c: Vertical(g3)
    c: Distance(g0) = 4
    c: Distance(g1) = 5.5
    c: DistanceY(g-1,g2) = 0.5
    c: DistanceX(g-1,g1) = 2
FEATURE [PartDesign::Pad] Pad003006
  Length = 10
  Length2 = 100
  Placement = pos=(0,44.2,0) rot=(0,0.707107,0.707107;3.14159rad)
  Reversed = true
  Sketch = -> Sketch045
  Type = 0
FEATURE [Part::Cut] Cut030
  Base = -> Cut026
  Tool = -> Pad003006
FEATURE [Part::Chamfer] Chamfer063
  Base = -> Fusion036
  Edges = 2 edges r=1.2: [Edge23,Edge24]
FEATURE [Part::Fillet] Fillet015
  Base = -> Chamfer063
  Edges = 4 edges r=1: [Edge34,Edge36,Edge39,Edge40]
FEATURE [Part::FeaturePython] Clone049  label="Clone of led-src"  # Draft clone (typed FeaturePython)
  Objects = -> [Fusion003]
  Placement = pos=(-16,-23,20) rot=(1,0,0;1.5708rad)
  Scale = (1,1,1)
FEATURE [Part::FeaturePython] Clone050  label="Clone of led-src001"  # Draft clone (typed FeaturePython)
  Objects = -> [Fusion003]
  Placement = pos=(-9.5,-23,20) rot=(1,0,0;1.5708rad)
  Scale = (1,1,1)
FEATURE [Part::FeaturePython] Clone051  label="Clone of led-src002"  # Draft clone (typed FeaturePython)
  Objects = -> [Fusion003]
  Placement = pos=(9.5,-23,20) rot=(1,0,0;1.5708rad)
  Scale = (1,1,1)
FEATURE [Part::FeaturePython] Clone052  label="Clone of led-src003"  # Draft clone (typed FeaturePython)
  Objects = -> [Fusion003]
  Placement = pos=(16,-23,20) rot=(1,0,0;1.5708rad)
  Scale = (1,1,1)
FEATURE [Part::Box] Box014  label="Cube013"
  Height = 2
  Length = 44
  Placement = pos=(-22,-27,15) rot=(0,0,1;0rad)
  Width = 50
FEATURE [Part::Fillet] Fillet016
  Base = -> Box014
  Edges = 2 edges r=1.5: [Edge3,Edge7]
FEATURE [Part::Feature] Polyline144
  Placement = pos=(-56.65,51,17) rot=(0,0,1;0rad)
  shape: bbox 42.42 x 50.72 x 2e-07 mm, 0 faces, 0 solids (baked)
FEATURE [Part::Cylinder] Cylinder048 .. Cylinder051  x4 (patterned run collapsed; names and placements below)
  Angle = 360
  Height = 10
  Radius = 1.75
  placements: 4 in arithmetic series — first pos=(0,6,-10) rot=(0,0,1;0rad), step (0,5,0), last pos=(0,21,-10) rot=(0,0,1;0rad)
FEATURE [Part::MultiFuse] Fusion037
  Shapes = -> [Cylinder051,Cylinder050,Cylinder049,Cylinder048]
FEATURE [Part::Cylinder] Cylinder052
  Angle = 360
  Height = 10
  Placement = pos=(-16.5,-3.5,24) rot=(0,0,1;0rad)
  Radius = 2.5
FEATURE [Part::Cylinder] Cylinder053
  Angle = 360
  Height = 10
  Placement = pos=(-16.5,-13.5,24) rot=(0,0,1;0rad)
  Radius = 2.5
FEATURE [Part::Cylinder] Cylinder054
  Angle = 360
  Height = 10
  Placement = pos=(16.5,-13.5,24) rot=(0,0,1;0rad)
  Radius = 2.5
FEATURE [Part::Cylinder] Cylinder055
  Angle = 360
  Height = 10
  Placement = pos=(16.5,-3.5,24) rot=(0,0,1;0rad)
  Radius = 2.5
FEATURE [Part::MultiFuse] Fusion038
  Shapes = -> [Cylinder053,Cylinder052,Cylinder055,Cylinder054]
FEATURE [Part::Cut] Cut032
  Base = -> Cut030
  Tool = -> Fusion038
FEATURE [Part::Box] Box015  label="Cube014"
  Height = 20
  Length = 9
  Placement = pos=(23,14,-1) rot=(0,0,1;0rad)
  Width = 16
FEATURE [Part::Box] Box016  label="Cube015"
  Height = 20
  Length = 9
  Placement = pos=(-32,14,-1) rot=(0,0,1;0rad)
  Width = 16
FEATURE [Part::Box] Box017  label="Cube016"
  Height = 28
  Length = 16
  Placement = pos=(17.5,9.5,-5) rot=(0,0,1;0rad)
  Width = 16
FEATURE [Part::Box] Box018  label="Cube017"
  Height = 28
  Length = 16
  Placement = pos=(-33.5,9.5,-5) rot=(0,0,1;0rad)
  Width = 16
FEATURE [Part::MultiFuse] Fusion039
  Shapes = -> [Box015,Box017,Box016,Box018]
FEATURE [Part::Cut] Cut033
  Base = -> Cut032
  Tool = -> Fusion039
FEATURE [Sketcher::SketchObject] Sketch046
  Placement = pos=(0,0,20) rot=(0,0,1;0rad)
  sketch-geometry (4):
    g0: LineSegment StartX=-18.9802 StartY=24.0676 StartZ=0 EndX=-33.2802 EndY=16.263 EndZ=0
    g1: LineSegment StartX=-33.2802 StartY=15.2224 StartZ=0 EndX=-18.9802 EndY=15.2224 EndZ=0
    g2: LineSegment StartX=-18.9802 StartY=15.2224 StartZ=0 EndX=-18.9802 EndY=24.0676 EndZ=0
    g3: LineSegment StartX=-33.2802 StartY=16.263 StartZ=0 EndX=-33.2802 EndY=15.2224 EndZ=0
  constraints (8):
    c: Horizontal(g1)
    c: Coincident(g1,g2)
    c: Coincident(g2,g0)
    c: Vertical(g2)
    c: DistanceX(g1,g1) = 14.3
    c: Coincident(g3,g0)
    c: Vertical(g3)
    c: Coincident(g1,g3)
FEATURE [PartDesign::Pad] Pad003007
  Length = 5
  Length2 = 100
  Placement = pos=(0,0,20) rot=(0,0,1;0rad)
  Sketch = -> Sketch046
  Type = 0
FEATURE [Part::Mirroring] Part__Mirroring010  label="Pad003007 (Mirror #11)"
  Base = (0,0,0)
  Normal = (1,0,0)
  Source = -> Pad003007
FEATURE [Part::MultiFuse] Fusion040
  Shapes = -> [Pad003007,Part__Mirroring010]
FEATURE [Part::Cut] Cut034
  Base = -> Cut033
  Tool = -> Fusion040
FEATURE [Part::Cylinder] Cylinder056
  Angle = 360
  Height = 10
  Placement = pos=(-18.5,-35,17.5) rot=(-1,0,0;1.5708rad)
  Radius = 1.85
FEATURE [Part::Cylinder] Cylinder057
  Angle = 360
  Height = 10
  Placement = pos=(-13.5,-35,17.5) rot=(-1,0,0;1.5708rad)
  Radius = 1.85
FEATURE [Part::Cylinder] Cylinder058
  Angle = 360
  Height = 10
  Placement = pos=(-8.5,-35,17.5) rot=(-1,0,0;1.5708rad)
  Radius = 1.85
FEATURE [Part::Cylinder] Cylinder059
  Angle = 360
  Height = 10
  Placement = pos=(13.5,-35,17.5) rot=(-1,0,0;1.5708rad)
  Radius = 1.85
FEATURE [Part::Cylinder] Cylinder060
  Angle = 360
  Height = 10
  Placement = pos=(18.5,-35,17.5) rot=(-1,0,0;1.5708rad)
  Radius = 1.85
FEATURE [Part::Cylinder] Cylinder061
  Angle = 360
  Height = 10
  Placement = pos=(8.5,-35,17.5) rot=(-1,0,0;1.5708rad)
  Radius = 1.85
FEATURE [Part::Box] Box019  label="Cube018"
  Height = 5
  Length = 11
  Placement = pos=(-5.5,-35,17) rot=(0,0,1;0rad)
  Width = 10
FEATURE [Part::Fillet] Fillet017
  Base = -> Box019
  Edges = 4 edges r=0.5: [Edge2,Edge4,Edge6,Edge8]
FEATURE [Part::MultiFuse] Fusion041
  Shapes = -> [Fillet017,Cylinder059,Cylinder056,Cylinder057,Cylinder058,Cylinder060,Cylinder061]
FEATURE [Part::Cut] Cut035
  Base = -> Fillet010
  Tool = -> Fusion041
FEATURE [Part::Cylinder] Cylinder062
  Angle = 360
  Height = 23
  Placement = pos=(-19.5,-37,15) rot=(-1,0,0;1.5708rad)
  Radius = 5.2
FEATURE [Part::Cylinder] Cylinder063
  Angle = 360
  Height = 21
  Placement = pos=(-15.5,18,-6) rot=(0,0,1;0rad)
  Radius = 3.5
FEATURE [Part::Cylinder] Cylinder064
  Angle = 360
  Height = 21
  Placement = pos=(-15.5,18,7) rot=(0,0,1;0rad)
  Radius = 1.65
FEATURE [Part::Cut] Cut037
  Base = -> Cylinder063
  Tool = -> Cylinder064
FEATURE [Part::Mirroring] Part__Mirroring011  label="Cut037 (Mirror #12)"
  Base = (0,0,0)
  Normal = (1,0,0)
  Source = -> Cut037
FEATURE [Part::MultiFuse] Fusion042
  Shapes = -> [Cut037,Part__Mirroring011]
FEATURE [Part::Cut] Cut038
  Base = -> Cut014
  Tool = -> Cylinder062
FEATURE [Part::Fillet] Fillet018
  Base = -> Cut038
  Edges = 2 edges r=1: [Edge25,Edge93]
FEATURE [Part::MultiFuse] Fusion043
  Shapes = -> [Fillet018,Fusion042]
FEATURE [Part::Chamfer] Chamfer064
  Base = -> Fusion043
  Edges = 2 edges r=1.5: [Edge69,Edge70]
FEATURE [Part::Cylinder] Cylinder065
  Angle = 360
  Height = 10
  Placement = pos=(0,10,0) rot=(0,0,1;0rad)
  Radius = 0.8
FEATURE [Part::Cylinder] Cylinder066
  Angle = 360
  Height = 10
  Placement = pos=(0,18,0) rot=(0,0,1;0rad)
  Radius = 0.8
FEATURE [Part::Cylinder] Cylinder067
  Angle = 360
  Height = 10
  Placement = pos=(0,26,0) rot=(0,0,1;0rad)
  Radius = 0.8
FEATURE [Part::MultiFuse] Fusion044
  Placement = pos=(0,0,-8) rot=(0,0,1;0rad)
  Shapes = -> [Cylinder067,Cylinder066,Cylinder065]
FEATURE [Part::Cut] Cut039
  Base = -> Chamfer064
  Tool = -> Fusion044
FEATURE [Part::MultiFuse] Fusion045
  Shapes = -> [Cut039,Pad003005]
FEATURE [Part::FeaturePython] Clone053  label="Clone of pushbuttonB"  # Draft clone (typed FeaturePython)
  Objects = -> [Clone047]
  Placement = pos=(-16.6,-13.4,17) rot=(0,0,1;0rad)
  Scale = (1,1,1)
FEATURE [Part::FeaturePython] Clone054  label="Clone of Compound"  # Draft clone (typed FeaturePython)
  Objects = -> [Compound]
  Placement = pos=(-16.6,-3.3,17) rot=(0,0,1;0rad)
  Scale = (1,1,1)
FEATURE [Part::Box] Box020  label="Cube019"
  Height = 5
  Length = 11
  Placement = pos=(-5.5,-35,17) rot=(0,0,1;0rad)
  Width = 10
FEATURE [Part::Fillet] Fillet019
  Base = -> Box020
  Edges = 4 edges r=0.5: [Edge2,Edge4,Edge6,Edge8]
  Placement = pos=(0,3.8,0) rot=(-1,0,0;1.5708rad)
FEATURE [Part::Cut] Cut040
  Base = -> Cut034
  Tool = -> Fillet019
